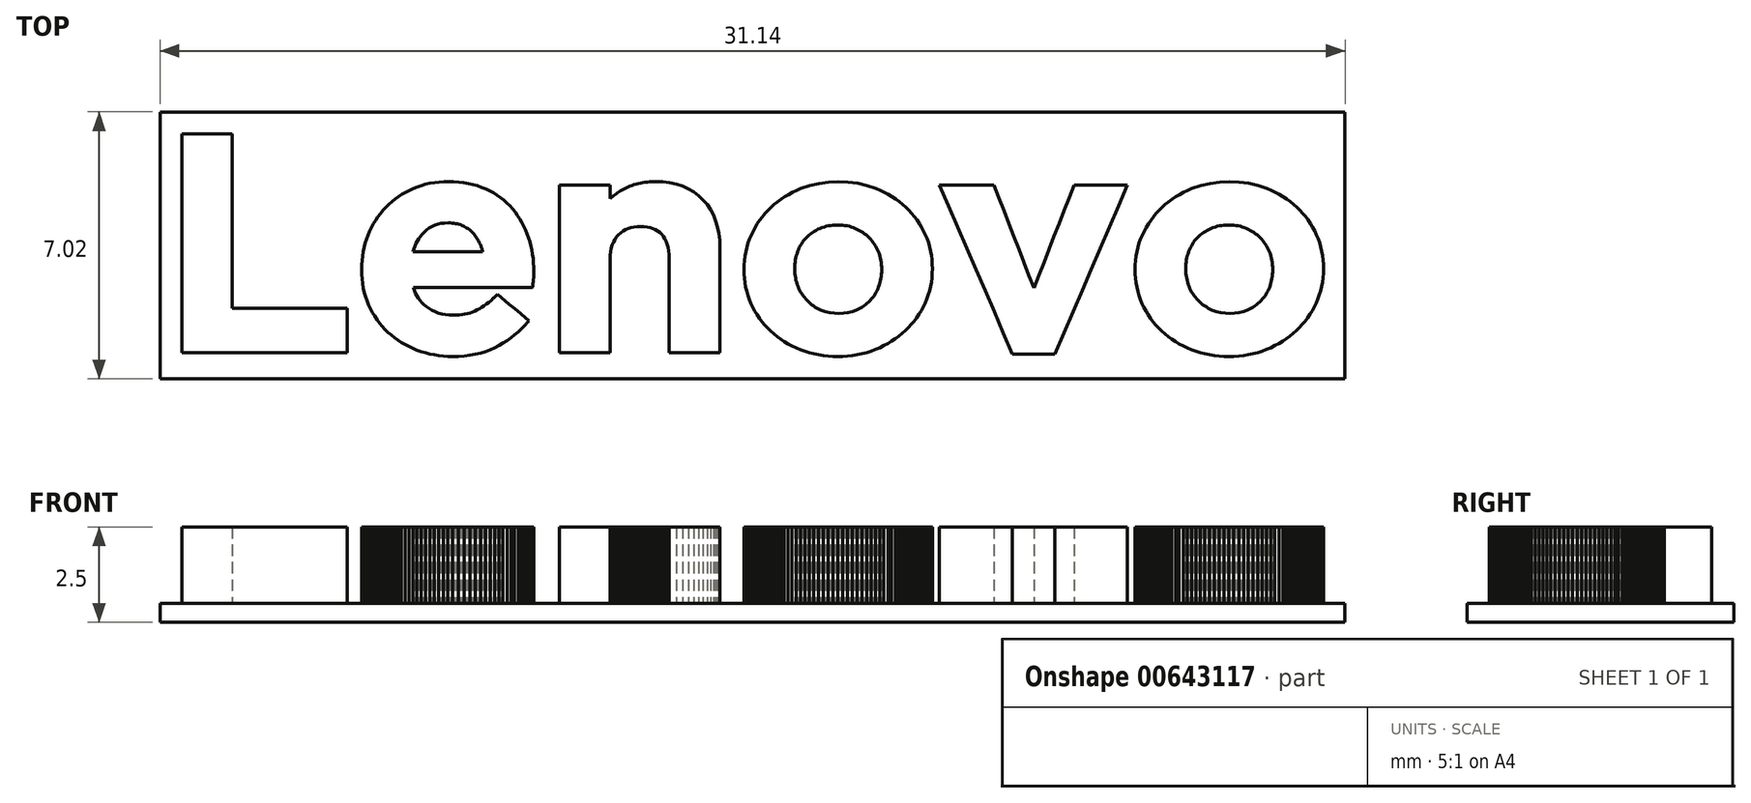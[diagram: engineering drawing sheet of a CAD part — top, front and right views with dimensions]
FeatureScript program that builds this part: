
annotation { "Feature Type Name" : "Feature", "Feature Type Description" : "" }
export const myFeature = defineFeature(function(context is Context, id is Id, definition is map)
    precondition{}
    {
        {
            var Q0;
            Q0=qCreatedBy(makeId("Top.planeOp"),FACE);
            var sketch = newSketch(context, id + "F0", { "sketchPlane" : qUnion([Q0])});
            skLineSegment(sketch, "E0", {"start": v(-13.67, -1.65) * mm, "end": v(-13.67, -1.08) * mm});
            skLineSegment(sketch, "E1", {"start": v(-13.67, -1.08) * mm, "end": v(-13.67, -0.5) * mm});
            skLineSegment(sketch, "E2", {"start": v(-13.67, -0.5) * mm, "end": v(-13.67, 0.06) * mm});
            skLineSegment(sketch, "E3", {"start": v(-13.67, 0.06) * mm, "end": v(-13.67, 0.64) * mm});
            skLineSegment(sketch, "E4", {"start": v(-13.67, 0.64) * mm, "end": v(-13.67, 1.2) * mm});
            skLineSegment(sketch, "E5", {"start": v(-13.67, 1.2) * mm, "end": v(-13.67, 1.78) * mm});
            skLineSegment(sketch, "E6", {"start": v(-13.67, 1.78) * mm, "end": v(-13.67, 2.35) * mm});
            skLineSegment(sketch, "E7", {"start": v(-13.67, 2.35) * mm, "end": v(-13.67, 2.92) * mm});
            skLineSegment(sketch, "E8", {"start": v(-13.67, 2.92) * mm, "end": v(-13.83, 2.92) * mm});
            skLineSegment(sketch, "E9", {"start": v(-13.83, 2.92) * mm, "end": v(-14, 2.92) * mm});
            skLineSegment(sketch, "E10", {"start": v(-14, 2.92) * mm, "end": v(-14.17, 2.92) * mm});
            skLineSegment(sketch, "E11", {"start": v(-14.17, 2.92) * mm, "end": v(-14.33, 2.92) * mm});
            skLineSegment(sketch, "E12", {"start": v(-14.33, 2.92) * mm, "end": v(-14.5, 2.92) * mm});
            skLineSegment(sketch, "E13", {"start": v(-14.5, 2.92) * mm, "end": v(-14.67, 2.92) * mm});
            skLineSegment(sketch, "E14", {"start": v(-14.67, 2.92) * mm, "end": v(-14.83, 2.92) * mm});
            skLineSegment(sketch, "E15", {"start": v(-14.83, 2.92) * mm, "end": v(-15, 2.92) * mm});
            skLineSegment(sketch, "E16", {"start": v(-15, 2.92) * mm, "end": v(-15, 2.2) * mm});
            skLineSegment(sketch, "E17", {"start": v(-15, 2.2) * mm, "end": v(-15, 1.49) * mm});
            skLineSegment(sketch, "E18", {"start": v(-15, 1.49) * mm, "end": v(-15, 0.77) * mm});
            skLineSegment(sketch, "E19", {"start": v(-15, 0.77) * mm, "end": v(-15, 0.05) * mm});
            skLineSegment(sketch, "E20", {"start": v(-15, 0.05) * mm, "end": v(-15, -0.67) * mm});
            skLineSegment(sketch, "E21", {"start": v(-15, -0.67) * mm, "end": v(-15, -1.4) * mm});
            skLineSegment(sketch, "E22", {"start": v(-15, -1.4) * mm, "end": v(-15, -2.11) * mm});
            skLineSegment(sketch, "E23", {"start": v(-15, -2.11) * mm, "end": v(-15, -2.83) * mm});
            skLineSegment(sketch, "E24", {"start": v(-15, -2.83) * mm, "end": v(-14.46, -2.83) * mm});
            skLineSegment(sketch, "E25", {"start": v(-14.46, -2.83) * mm, "end": v(-13.91, -2.83) * mm});
            skLineSegment(sketch, "E26", {"start": v(-13.91, -2.83) * mm, "end": v(-13.37, -2.83) * mm});
            skLineSegment(sketch, "E27", {"start": v(-13.37, -2.83) * mm, "end": v(-12.82, -2.83) * mm});
            skLineSegment(sketch, "E28", {"start": v(-12.82, -2.83) * mm, "end": v(-12.28, -2.83) * mm});
            skLineSegment(sketch, "E29", {"start": v(-12.28, -2.83) * mm, "end": v(-11.74, -2.83) * mm});
            skLineSegment(sketch, "E30", {"start": v(-11.74, -2.83) * mm, "end": v(-11.2, -2.83) * mm});
            skLineSegment(sketch, "E31", {"start": v(-11.2, -2.83) * mm, "end": v(-10.65, -2.83) * mm});
            skLineSegment(sketch, "E32", {"start": v(-10.65, -2.83) * mm, "end": v(-10.65, -2.68) * mm});
            skLineSegment(sketch, "E33", {"start": v(-10.65, -2.68) * mm, "end": v(-10.65, -2.54) * mm});
            skLineSegment(sketch, "E34", {"start": v(-10.65, -2.54) * mm, "end": v(-10.65, -2.39) * mm});
            skLineSegment(sketch, "E35", {"start": v(-10.65, -2.39) * mm, "end": v(-10.65, -2.24) * mm});
            skLineSegment(sketch, "E36", {"start": v(-10.65, -2.24) * mm, "end": v(-10.65, -2.1) * mm});
            skLineSegment(sketch, "E37", {"start": v(-10.65, -2.1) * mm, "end": v(-10.65, -1.95) * mm});
            skLineSegment(sketch, "E38", {"start": v(-10.65, -1.95) * mm, "end": v(-10.65, -1.8) * mm});
            skLineSegment(sketch, "E39", {"start": v(-10.65, -1.8) * mm, "end": v(-10.65, -1.65) * mm});
            skLineSegment(sketch, "E40", {"start": v(-10.65, -1.65) * mm, "end": v(-11.02, -1.65) * mm});
            skLineSegment(sketch, "E41", {"start": v(-11.02, -1.65) * mm, "end": v(-11.4, -1.65) * mm});
            skLineSegment(sketch, "E42", {"start": v(-11.4, -1.65) * mm, "end": v(-11.78, -1.65) * mm});
            skLineSegment(sketch, "E43", {"start": v(-11.78, -1.65) * mm, "end": v(-12.16, -1.65) * mm});
            skLineSegment(sketch, "E44", {"start": v(-12.16, -1.65) * mm, "end": v(-12.54, -1.65) * mm});
            skLineSegment(sketch, "E45", {"start": v(-12.54, -1.65) * mm, "end": v(-12.91, -1.65) * mm});
            skLineSegment(sketch, "E46", {"start": v(-12.91, -1.65) * mm, "end": v(-13.3, -1.65) * mm});
            skLineSegment(sketch, "E47", {"start": v(-13.3, -1.65) * mm, "end": v(-13.67, -1.65) * mm});
            skLineSegment(sketch, "E48", {"start": v(-7.1, -0.18) * mm, "end": v(-7.32, -0.18) * mm});
            skLineSegment(sketch, "E49", {"start": v(-7.32, -0.18) * mm, "end": v(-7.55, -0.18) * mm});
            skLineSegment(sketch, "E50", {"start": v(-7.55, -0.18) * mm, "end": v(-7.78, -0.18) * mm});
            skLineSegment(sketch, "E51", {"start": v(-7.78, -0.18) * mm, "end": v(-8, -0.18) * mm});
            skLineSegment(sketch, "E52", {"start": v(-8, -0.18) * mm, "end": v(-8.24, -0.18) * mm});
            skLineSegment(sketch, "E53", {"start": v(-8.24, -0.18) * mm, "end": v(-8.47, -0.18) * mm});
            skLineSegment(sketch, "E54", {"start": v(-8.47, -0.18) * mm, "end": v(-8.7, -0.18) * mm});
            skLineSegment(sketch, "E55", {"start": v(-8.7, -0.18) * mm, "end": v(-8.92, -0.18) * mm});
            skLineSegment(sketch, "E56", {"start": v(-8.92, -0.18) * mm, "end": v(-8.9, -0.1) * mm});
            skLineSegment(sketch, "E57", {"start": v(-8.9, -0.1) * mm, "end": v(-8.88, -0.03) * mm});
            skLineSegment(sketch, "E58", {"start": v(-8.88, -0.03) * mm, "end": v(-8.85, 0.04) * mm});
            skLineSegment(sketch, "E59", {"start": v(-8.85, 0.04) * mm, "end": v(-8.81, 0.1) * mm});
            skLineSegment(sketch, "E60", {"start": v(-8.81, 0.1) * mm, "end": v(-8.77, 0.17) * mm});
            skLineSegment(sketch, "E61", {"start": v(-8.77, 0.17) * mm, "end": v(-8.73, 0.23) * mm});
            skLineSegment(sketch, "E62", {"start": v(-8.73, 0.23) * mm, "end": v(-8.69, 0.29) * mm});
            skLineSegment(sketch, "E63", {"start": v(-8.69, 0.29) * mm, "end": v(-8.64, 0.34) * mm});
            skLineSegment(sketch, "E64", {"start": v(-8.64, 0.34) * mm, "end": v(-8.57, 0.4) * mm});
            skLineSegment(sketch, "E65", {"start": v(-8.57, 0.4) * mm, "end": v(-8.5, 0.45) * mm});
            skLineSegment(sketch, "E66", {"start": v(-8.5, 0.45) * mm, "end": v(-8.43, 0.5) * mm});
            skLineSegment(sketch, "E67", {"start": v(-8.43, 0.5) * mm, "end": v(-8.35, 0.53) * mm});
            skLineSegment(sketch, "E68", {"start": v(-8.35, 0.53) * mm, "end": v(-8.27, 0.55) * mm});
            skLineSegment(sketch, "E69", {"start": v(-8.27, 0.55) * mm, "end": v(-8.19, 0.57) * mm});
            skLineSegment(sketch, "E70", {"start": v(-8.19, 0.57) * mm, "end": v(-8.1, 0.58) * mm});
            skLineSegment(sketch, "E71", {"start": v(-8.1, 0.58) * mm, "end": v(-8, 0.59) * mm});
            skLineSegment(sketch, "E72", {"start": v(-8, 0.59) * mm, "end": v(-7.95, 0.59) * mm});
            skLineSegment(sketch, "E73", {"start": v(-7.95, 0.59) * mm, "end": v(-7.9, 0.58) * mm});
            skLineSegment(sketch, "E74", {"start": v(-7.9, 0.58) * mm, "end": v(-7.85, 0.58) * mm});
            skLineSegment(sketch, "E75", {"start": v(-7.85, 0.58) * mm, "end": v(-7.8, 0.57) * mm});
            skLineSegment(sketch, "E76", {"start": v(-7.8, 0.57) * mm, "end": v(-7.76, 0.56) * mm});
            skLineSegment(sketch, "E77", {"start": v(-7.76, 0.56) * mm, "end": v(-7.71, 0.55) * mm});
            skLineSegment(sketch, "E78", {"start": v(-7.71, 0.55) * mm, "end": v(-7.67, 0.53) * mm});
            skLineSegment(sketch, "E79", {"start": v(-7.67, 0.53) * mm, "end": v(-7.63, 0.52) * mm});
            skLineSegment(sketch, "E80", {"start": v(-7.63, 0.52) * mm, "end": v(-7.59, 0.5) * mm});
            skLineSegment(sketch, "E81", {"start": v(-7.59, 0.5) * mm, "end": v(-7.55, 0.48) * mm});
            skLineSegment(sketch, "E82", {"start": v(-7.55, 0.48) * mm, "end": v(-7.51, 0.46) * mm});
            skLineSegment(sketch, "E83", {"start": v(-7.51, 0.46) * mm, "end": v(-7.48, 0.43) * mm});
            skLineSegment(sketch, "E84", {"start": v(-7.48, 0.43) * mm, "end": v(-7.44, 0.4) * mm});
            skLineSegment(sketch, "E85", {"start": v(-7.44, 0.4) * mm, "end": v(-7.41, 0.38) * mm});
            skLineSegment(sketch, "E86", {"start": v(-7.41, 0.38) * mm, "end": v(-7.38, 0.35) * mm});
            skLineSegment(sketch, "E87", {"start": v(-7.38, 0.35) * mm, "end": v(-7.35, 0.32) * mm});
            skLineSegment(sketch, "E88", {"start": v(-7.35, 0.32) * mm, "end": v(-7.32, 0.3) * mm});
            skLineSegment(sketch, "E89", {"start": v(-7.32, 0.3) * mm, "end": v(-7.3, 0.26) * mm});
            skLineSegment(sketch, "E90", {"start": v(-7.3, 0.26) * mm, "end": v(-7.27, 0.23) * mm});
            skLineSegment(sketch, "E91", {"start": v(-7.27, 0.23) * mm, "end": v(-7.24, 0.2) * mm});
            skLineSegment(sketch, "E92", {"start": v(-7.24, 0.2) * mm, "end": v(-7.22, 0.15) * mm});
            skLineSegment(sketch, "E93", {"start": v(-7.22, 0.15) * mm, "end": v(-7.2, 0.11) * mm});
            skLineSegment(sketch, "E94", {"start": v(-7.2, 0.11) * mm, "end": v(-7.18, 0.07) * mm});
            skLineSegment(sketch, "E95", {"start": v(-7.18, 0.07) * mm, "end": v(-7.16, 0.03) * mm});
            skLineSegment(sketch, "E96", {"start": v(-7.16, 0.03) * mm, "end": v(-7.15, 0) * mm});
            skLineSegment(sketch, "E97", {"start": v(-7.15, 0) * mm, "end": v(-7.14, -0.02) * mm});
            skLineSegment(sketch, "E98", {"start": v(-7.14, -0.02) * mm, "end": v(-7.13, -0.04) * mm});
            skLineSegment(sketch, "E99", {"start": v(-7.13, -0.04) * mm, "end": v(-7.12, -0.07) * mm});
            skLineSegment(sketch, "E100", {"start": v(-7.12, -0.07) * mm, "end": v(-7.11, -0.1) * mm});
            skLineSegment(sketch, "E101", {"start": v(-7.11, -0.1) * mm, "end": v(-7.1, -0.12) * mm});
            skLineSegment(sketch, "E102", {"start": v(-7.1, -0.12) * mm, "end": v(-7.1, -0.15) * mm});
            skLineSegment(sketch, "E103", {"start": v(-7.1, -0.15) * mm, "end": v(-7.1, -0.18) * mm});
            skLineSegment(sketch, "E104", {"start": v(-5.89, 0.2) * mm, "end": v(-5.92, 0.3) * mm});
            skLineSegment(sketch, "E105", {"start": v(-5.92, 0.3) * mm, "end": v(-5.96, 0.4) * mm});
            skLineSegment(sketch, "E106", {"start": v(-5.96, 0.4) * mm, "end": v(-6.01, 0.5) * mm});
            skLineSegment(sketch, "E107", {"start": v(-6.01, 0.5) * mm, "end": v(-6.06, 0.6) * mm});
            skLineSegment(sketch, "E108", {"start": v(-6.06, 0.6) * mm, "end": v(-6.12, 0.7) * mm});
            skLineSegment(sketch, "E109", {"start": v(-6.12, 0.7) * mm, "end": v(-6.17, 0.78) * mm});
            skLineSegment(sketch, "E110", {"start": v(-6.17, 0.78) * mm, "end": v(-6.24, 0.87) * mm});
            skLineSegment(sketch, "E111", {"start": v(-6.24, 0.87) * mm, "end": v(-6.3, 0.95) * mm});
            skLineSegment(sketch, "E112", {"start": v(-6.3, 0.95) * mm, "end": v(-6.38, 1.03) * mm});
            skLineSegment(sketch, "E113", {"start": v(-6.38, 1.03) * mm, "end": v(-6.45, 1.11) * mm});
            skLineSegment(sketch, "E114", {"start": v(-6.45, 1.11) * mm, "end": v(-6.54, 1.18) * mm});
            skLineSegment(sketch, "E115", {"start": v(-6.54, 1.18) * mm, "end": v(-6.62, 1.25) * mm});
            skLineSegment(sketch, "E116", {"start": v(-6.62, 1.25) * mm, "end": v(-6.71, 1.31) * mm});
            skLineSegment(sketch, "E117", {"start": v(-6.71, 1.31) * mm, "end": v(-6.8, 1.37) * mm});
            skLineSegment(sketch, "E118", {"start": v(-6.8, 1.37) * mm, "end": v(-6.9, 1.43) * mm});
            skLineSegment(sketch, "E119", {"start": v(-6.9, 1.43) * mm, "end": v(-7.01, 1.48) * mm});
            skLineSegment(sketch, "E120", {"start": v(-7.01, 1.48) * mm, "end": v(-7.12, 1.52) * mm});
            skLineSegment(sketch, "E121", {"start": v(-7.12, 1.52) * mm, "end": v(-7.23, 1.56) * mm});
            skLineSegment(sketch, "E122", {"start": v(-7.23, 1.56) * mm, "end": v(-7.35, 1.6) * mm});
            skLineSegment(sketch, "E123", {"start": v(-7.35, 1.6) * mm, "end": v(-7.47, 1.62) * mm});
            skLineSegment(sketch, "E124", {"start": v(-7.47, 1.62) * mm, "end": v(-7.6, 1.65) * mm});
            skLineSegment(sketch, "E125", {"start": v(-7.6, 1.65) * mm, "end": v(-7.72, 1.66) * mm});
            skLineSegment(sketch, "E126", {"start": v(-7.72, 1.66) * mm, "end": v(-7.85, 1.67) * mm});
            skLineSegment(sketch, "E127", {"start": v(-7.85, 1.67) * mm, "end": v(-7.99, 1.67) * mm});
            skLineSegment(sketch, "E128", {"start": v(-7.99, 1.67) * mm, "end": v(-8.11, 1.67) * mm});
            skLineSegment(sketch, "E129", {"start": v(-8.11, 1.67) * mm, "end": v(-8.24, 1.66) * mm});
            skLineSegment(sketch, "E130", {"start": v(-8.24, 1.66) * mm, "end": v(-8.36, 1.65) * mm});
            skLineSegment(sketch, "E131", {"start": v(-8.36, 1.65) * mm, "end": v(-8.47, 1.63) * mm});
            skLineSegment(sketch, "E132", {"start": v(-8.47, 1.63) * mm, "end": v(-8.59, 1.6) * mm});
            skLineSegment(sketch, "E133", {"start": v(-8.59, 1.6) * mm, "end": v(-8.7, 1.57) * mm});
            skLineSegment(sketch, "E134", {"start": v(-8.7, 1.57) * mm, "end": v(-8.8, 1.53) * mm});
            skLineSegment(sketch, "E135", {"start": v(-8.8, 1.53) * mm, "end": v(-8.91, 1.5) * mm});
            skLineSegment(sketch, "E136", {"start": v(-8.91, 1.5) * mm, "end": v(-9.02, 1.44) * mm});
            skLineSegment(sketch, "E137", {"start": v(-9.02, 1.44) * mm, "end": v(-9.11, 1.4) * mm});
            skLineSegment(sketch, "E138", {"start": v(-9.11, 1.4) * mm, "end": v(-9.2, 1.34) * mm});
            skLineSegment(sketch, "E139", {"start": v(-9.2, 1.34) * mm, "end": v(-9.3, 1.28) * mm});
            skLineSegment(sketch, "E140", {"start": v(-9.3, 1.28) * mm, "end": v(-9.4, 1.21) * mm});
            skLineSegment(sketch, "E141", {"start": v(-9.4, 1.21) * mm, "end": v(-9.48, 1.14) * mm});
            skLineSegment(sketch, "E142", {"start": v(-9.48, 1.14) * mm, "end": v(-9.56, 1.07) * mm});
            skLineSegment(sketch, "E143", {"start": v(-9.56, 1.07) * mm, "end": v(-9.64, 1) * mm});
            skLineSegment(sketch, "E144", {"start": v(-9.64, 1) * mm, "end": v(-9.7, 0.92) * mm});
            skLineSegment(sketch, "E145", {"start": v(-9.7, 0.92) * mm, "end": v(-9.78, 0.83) * mm});
            skLineSegment(sketch, "E146", {"start": v(-9.78, 0.83) * mm, "end": v(-9.84, 0.75) * mm});
            skLineSegment(sketch, "E147", {"start": v(-9.84, 0.75) * mm, "end": v(-9.9, 0.66) * mm});
            skLineSegment(sketch, "E148", {"start": v(-9.9, 0.66) * mm, "end": v(-9.96, 0.56) * mm});
            skLineSegment(sketch, "E149", {"start": v(-9.96, 0.56) * mm, "end": v(-10.02, 0.47) * mm});
            skLineSegment(sketch, "E150", {"start": v(-10.02, 0.47) * mm, "end": v(-10.06, 0.37) * mm});
            skLineSegment(sketch, "E151", {"start": v(-10.06, 0.37) * mm, "end": v(-10.1, 0.27) * mm});
            skLineSegment(sketch, "E152", {"start": v(-10.1, 0.27) * mm, "end": v(-10.15, 0.16) * mm});
            skLineSegment(sketch, "E153", {"start": v(-10.15, 0.16) * mm, "end": v(-10.18, 0.05) * mm});
            skLineSegment(sketch, "E154", {"start": v(-10.18, 0.05) * mm, "end": v(-10.2, -0.05) * mm});
            skLineSegment(sketch, "E155", {"start": v(-10.2, -0.05) * mm, "end": v(-10.23, -0.17) * mm});
            skLineSegment(sketch, "E156", {"start": v(-10.23, -0.17) * mm, "end": v(-10.25, -0.28) * mm});
            skLineSegment(sketch, "E157", {"start": v(-10.25, -0.28) * mm, "end": v(-10.26, -0.4) * mm});
            skLineSegment(sketch, "E158", {"start": v(-10.26, -0.4) * mm, "end": v(-10.27, -0.52) * mm});
            skLineSegment(sketch, "E159", {"start": v(-10.27, -0.52) * mm, "end": v(-10.27, -0.64) * mm});
            skLineSegment(sketch, "E160", {"start": v(-10.27, -0.64) * mm, "end": v(-10.27, -0.76) * mm});
            skLineSegment(sketch, "E161", {"start": v(-10.27, -0.76) * mm, "end": v(-10.26, -0.88) * mm});
            skLineSegment(sketch, "E162", {"start": v(-10.26, -0.88) * mm, "end": v(-10.25, -1) * mm});
            skLineSegment(sketch, "E163", {"start": v(-10.25, -1) * mm, "end": v(-10.23, -1.12) * mm});
            skLineSegment(sketch, "E164", {"start": v(-10.23, -1.12) * mm, "end": v(-10.2, -1.24) * mm});
            skLineSegment(sketch, "E165", {"start": v(-10.2, -1.24) * mm, "end": v(-10.17, -1.35) * mm});
            skLineSegment(sketch, "E166", {"start": v(-10.17, -1.35) * mm, "end": v(-10.13, -1.46) * mm});
            skLineSegment(sketch, "E167", {"start": v(-10.13, -1.46) * mm, "end": v(-10.1, -1.56) * mm});
            skLineSegment(sketch, "E168", {"start": v(-10.1, -1.56) * mm, "end": v(-10.04, -1.67) * mm});
            skLineSegment(sketch, "E169", {"start": v(-10.04, -1.67) * mm, "end": v(-9.99, -1.77) * mm});
            skLineSegment(sketch, "E170", {"start": v(-9.99, -1.77) * mm, "end": v(-9.93, -1.86) * mm});
            skLineSegment(sketch, "E171", {"start": v(-9.93, -1.86) * mm, "end": v(-9.87, -1.96) * mm});
            skLineSegment(sketch, "E172", {"start": v(-9.87, -1.96) * mm, "end": v(-9.8, -2.04) * mm});
            skLineSegment(sketch, "E173", {"start": v(-9.8, -2.04) * mm, "end": v(-9.73, -2.13) * mm});
            skLineSegment(sketch, "E174", {"start": v(-9.73, -2.13) * mm, "end": v(-9.66, -2.21) * mm});
            skLineSegment(sketch, "E175", {"start": v(-9.66, -2.21) * mm, "end": v(-9.58, -2.29) * mm});
            skLineSegment(sketch, "E176", {"start": v(-9.58, -2.29) * mm, "end": v(-9.5, -2.36) * mm});
            skLineSegment(sketch, "E177", {"start": v(-9.5, -2.36) * mm, "end": v(-9.41, -2.43) * mm});
            skLineSegment(sketch, "E178", {"start": v(-9.41, -2.43) * mm, "end": v(-9.32, -2.5) * mm});
            skLineSegment(sketch, "E179", {"start": v(-9.32, -2.5) * mm, "end": v(-9.23, -2.56) * mm});
            skLineSegment(sketch, "E180", {"start": v(-9.23, -2.56) * mm, "end": v(-9.13, -2.61) * mm});
            skLineSegment(sketch, "E181", {"start": v(-9.13, -2.61) * mm, "end": v(-9.03, -2.66) * mm});
            skLineSegment(sketch, "E182", {"start": v(-9.03, -2.66) * mm, "end": v(-8.93, -2.71) * mm});
            skLineSegment(sketch, "E183", {"start": v(-8.93, -2.71) * mm, "end": v(-8.82, -2.76) * mm});
            skLineSegment(sketch, "E184", {"start": v(-8.82, -2.76) * mm, "end": v(-8.7, -2.8) * mm});
            skLineSegment(sketch, "E185", {"start": v(-8.7, -2.8) * mm, "end": v(-8.6, -2.83) * mm});
            skLineSegment(sketch, "E186", {"start": v(-8.6, -2.83) * mm, "end": v(-8.48, -2.86) * mm});
            skLineSegment(sketch, "E187", {"start": v(-8.48, -2.86) * mm, "end": v(-8.37, -2.88) * mm});
            skLineSegment(sketch, "E188", {"start": v(-8.37, -2.88) * mm, "end": v(-8.25, -2.9) * mm});
            skLineSegment(sketch, "E189", {"start": v(-8.25, -2.9) * mm, "end": v(-8.13, -2.91) * mm});
            skLineSegment(sketch, "E190", {"start": v(-8.13, -2.91) * mm, "end": v(-8, -2.92) * mm});
            skLineSegment(sketch, "E191", {"start": v(-8, -2.92) * mm, "end": v(-7.88, -2.92) * mm});
            skLineSegment(sketch, "E192", {"start": v(-7.88, -2.92) * mm, "end": v(-7.73, -2.92) * mm});
            skLineSegment(sketch, "E193", {"start": v(-7.73, -2.92) * mm, "end": v(-7.57, -2.9) * mm});
            skLineSegment(sketch, "E194", {"start": v(-7.57, -2.9) * mm, "end": v(-7.43, -2.9) * mm});
            skLineSegment(sketch, "E195", {"start": v(-7.43, -2.9) * mm, "end": v(-7.29, -2.87) * mm});
            skLineSegment(sketch, "E196", {"start": v(-7.29, -2.87) * mm, "end": v(-7.15, -2.83) * mm});
            skLineSegment(sketch, "E197", {"start": v(-7.15, -2.83) * mm, "end": v(-7.02, -2.8) * mm});
            skLineSegment(sketch, "E198", {"start": v(-7.02, -2.8) * mm, "end": v(-6.9, -2.75) * mm});
            skLineSegment(sketch, "E199", {"start": v(-6.9, -2.75) * mm, "end": v(-6.78, -2.7) * mm});
            skLineSegment(sketch, "E200", {"start": v(-6.78, -2.7) * mm, "end": v(-6.66, -2.64) * mm});
            skLineSegment(sketch, "E201", {"start": v(-6.66, -2.64) * mm, "end": v(-6.56, -2.57) * mm});
            skLineSegment(sketch, "E202", {"start": v(-6.56, -2.57) * mm, "end": v(-6.45, -2.5) * mm});
            skLineSegment(sketch, "E203", {"start": v(-6.45, -2.5) * mm, "end": v(-6.35, -2.43) * mm});
            skLineSegment(sketch, "E204", {"start": v(-6.35, -2.43) * mm, "end": v(-6.25, -2.36) * mm});
            skLineSegment(sketch, "E205", {"start": v(-6.25, -2.36) * mm, "end": v(-6.16, -2.28) * mm});
            skLineSegment(sketch, "E206", {"start": v(-6.16, -2.28) * mm, "end": v(-6.07, -2.19) * mm});
            skLineSegment(sketch, "E207", {"start": v(-6.07, -2.19) * mm, "end": v(-5.98, -2.1) * mm});
            skLineSegment(sketch, "E208", {"start": v(-5.98, -2.1) * mm, "end": v(-5.97, -2.08) * mm});
            skLineSegment(sketch, "E209", {"start": v(-5.97, -2.08) * mm, "end": v(-5.96, -2.07) * mm});
            skLineSegment(sketch, "E210", {"start": v(-5.96, -2.07) * mm, "end": v(-5.94, -2.06) * mm});
            skLineSegment(sketch, "E211", {"start": v(-5.94, -2.06) * mm, "end": v(-5.93, -2.04) * mm});
            skLineSegment(sketch, "E212", {"start": v(-5.93, -2.04) * mm, "end": v(-5.92, -2.03) * mm});
            skLineSegment(sketch, "E213", {"start": v(-5.92, -2.03) * mm, "end": v(-5.9, -2.01) * mm});
            skLineSegment(sketch, "E214", {"start": v(-5.9, -2.01) * mm, "end": v(-5.9, -2) * mm});
            skLineSegment(sketch, "E215", {"start": v(-5.9, -2) * mm, "end": v(-5.88, -1.98) * mm});
            skLineSegment(sketch, "E216", {"start": v(-5.88, -1.98) * mm, "end": v(-5.98, -1.9) * mm});
            skLineSegment(sketch, "E217", {"start": v(-5.98, -1.9) * mm, "end": v(-6.08, -1.8) * mm});
            skLineSegment(sketch, "E218", {"start": v(-6.08, -1.8) * mm, "end": v(-6.19, -1.72) * mm});
            skLineSegment(sketch, "E219", {"start": v(-6.19, -1.72) * mm, "end": v(-6.29, -1.64) * mm});
            skLineSegment(sketch, "E220", {"start": v(-6.29, -1.64) * mm, "end": v(-6.4, -1.55) * mm});
            skLineSegment(sketch, "E221", {"start": v(-6.4, -1.55) * mm, "end": v(-6.5, -1.46) * mm});
            skLineSegment(sketch, "E222", {"start": v(-6.5, -1.46) * mm, "end": v(-6.6, -1.38) * mm});
            skLineSegment(sketch, "E223", {"start": v(-6.6, -1.38) * mm, "end": v(-6.7, -1.3) * mm});
            skLineSegment(sketch, "E224", {"start": v(-6.7, -1.3) * mm, "end": v(-6.71, -1.3) * mm});
            skLineSegment(sketch, "E225", {"start": v(-6.71, -1.3) * mm, "end": v(-6.73, -1.32) * mm});
            skLineSegment(sketch, "E226", {"start": v(-6.73, -1.32) * mm, "end": v(-6.74, -1.33) * mm});
            skLineSegment(sketch, "E227", {"start": v(-6.74, -1.33) * mm, "end": v(-6.75, -1.34) * mm});
            skLineSegment(sketch, "E228", {"start": v(-6.75, -1.34) * mm, "end": v(-6.77, -1.36) * mm});
            skLineSegment(sketch, "E229", {"start": v(-6.77, -1.36) * mm, "end": v(-6.78, -1.37) * mm});
            skLineSegment(sketch, "E230", {"start": v(-6.78, -1.37) * mm, "end": v(-6.8, -1.38) * mm});
            skLineSegment(sketch, "E231", {"start": v(-6.8, -1.38) * mm, "end": v(-6.8, -1.4) * mm});
            skLineSegment(sketch, "E232", {"start": v(-6.8, -1.4) * mm, "end": v(-6.87, -1.45) * mm});
            skLineSegment(sketch, "E233", {"start": v(-6.87, -1.45) * mm, "end": v(-6.93, -1.5) * mm});
            skLineSegment(sketch, "E234", {"start": v(-6.93, -1.5) * mm, "end": v(-7, -1.55) * mm});
            skLineSegment(sketch, "E235", {"start": v(-7, -1.55) * mm, "end": v(-7.05, -1.6) * mm});
            skLineSegment(sketch, "E236", {"start": v(-7.05, -1.6) * mm, "end": v(-7.11, -1.63) * mm});
            skLineSegment(sketch, "E237", {"start": v(-7.11, -1.63) * mm, "end": v(-7.18, -1.67) * mm});
            skLineSegment(sketch, "E238", {"start": v(-7.18, -1.67) * mm, "end": v(-7.24, -1.7) * mm});
            skLineSegment(sketch, "E239", {"start": v(-7.24, -1.7) * mm, "end": v(-7.3, -1.73) * mm});
            skLineSegment(sketch, "E240", {"start": v(-7.3, -1.73) * mm, "end": v(-7.36, -1.76) * mm});
            skLineSegment(sketch, "E241", {"start": v(-7.36, -1.76) * mm, "end": v(-7.42, -1.78) * mm});
            skLineSegment(sketch, "E242", {"start": v(-7.42, -1.78) * mm, "end": v(-7.49, -1.8) * mm});
            skLineSegment(sketch, "E243", {"start": v(-7.49, -1.8) * mm, "end": v(-7.56, -1.81) * mm});
            skLineSegment(sketch, "E244", {"start": v(-7.56, -1.81) * mm, "end": v(-7.63, -1.82) * mm});
            skLineSegment(sketch, "E245", {"start": v(-7.63, -1.82) * mm, "end": v(-7.7, -1.83) * mm});
            skLineSegment(sketch, "E246", {"start": v(-7.7, -1.83) * mm, "end": v(-7.79, -1.84) * mm});
            skLineSegment(sketch, "E247", {"start": v(-7.79, -1.84) * mm, "end": v(-7.87, -1.84) * mm});
            skLineSegment(sketch, "E248", {"start": v(-7.87, -1.84) * mm, "end": v(-7.97, -1.84) * mm});
            skLineSegment(sketch, "E249", {"start": v(-7.97, -1.84) * mm, "end": v(-8.07, -1.82) * mm});
            skLineSegment(sketch, "E250", {"start": v(-8.07, -1.82) * mm, "end": v(-8.17, -1.8) * mm});
            skLineSegment(sketch, "E251", {"start": v(-8.17, -1.8) * mm, "end": v(-8.26, -1.78) * mm});
            skLineSegment(sketch, "E252", {"start": v(-8.26, -1.78) * mm, "end": v(-8.35, -1.75) * mm});
            skLineSegment(sketch, "E253", {"start": v(-8.35, -1.75) * mm, "end": v(-8.43, -1.7) * mm});
            skLineSegment(sketch, "E254", {"start": v(-8.43, -1.7) * mm, "end": v(-8.5, -1.66) * mm});
            skLineSegment(sketch, "E255", {"start": v(-8.5, -1.66) * mm, "end": v(-8.58, -1.6) * mm});
            skLineSegment(sketch, "E256", {"start": v(-8.58, -1.6) * mm, "end": v(-8.64, -1.56) * mm});
            skLineSegment(sketch, "E257", {"start": v(-8.64, -1.56) * mm, "end": v(-8.7, -1.5) * mm});
            skLineSegment(sketch, "E258", {"start": v(-8.7, -1.5) * mm, "end": v(-8.74, -1.45) * mm});
            skLineSegment(sketch, "E259", {"start": v(-8.74, -1.45) * mm, "end": v(-8.78, -1.4) * mm});
            skLineSegment(sketch, "E260", {"start": v(-8.78, -1.4) * mm, "end": v(-8.82, -1.33) * mm});
            skLineSegment(sketch, "E261", {"start": v(-8.82, -1.33) * mm, "end": v(-8.85, -1.26) * mm});
            skLineSegment(sketch, "E262", {"start": v(-8.85, -1.26) * mm, "end": v(-8.88, -1.19) * mm});
            skLineSegment(sketch, "E263", {"start": v(-8.88, -1.19) * mm, "end": v(-8.91, -1.11) * mm});
            skLineSegment(sketch, "E264", {"start": v(-8.91, -1.11) * mm, "end": v(-8.52, -1.11) * mm});
            skLineSegment(sketch, "E265", {"start": v(-8.52, -1.11) * mm, "end": v(-8.13, -1.11) * mm});
            skLineSegment(sketch, "E266", {"start": v(-8.13, -1.11) * mm, "end": v(-7.74, -1.11) * mm});
            skLineSegment(sketch, "E267", {"start": v(-7.74, -1.11) * mm, "end": v(-7.35, -1.11) * mm});
            skLineSegment(sketch, "E268", {"start": v(-7.35, -1.11) * mm, "end": v(-6.96, -1.11) * mm});
            skLineSegment(sketch, "E269", {"start": v(-6.96, -1.11) * mm, "end": v(-6.56, -1.11) * mm});
            skLineSegment(sketch, "E270", {"start": v(-6.56, -1.11) * mm, "end": v(-6.17, -1.11) * mm});
            skLineSegment(sketch, "E271", {"start": v(-6.17, -1.11) * mm, "end": v(-5.78, -1.11) * mm});
            skLineSegment(sketch, "E272", {"start": v(-5.78, -1.11) * mm, "end": v(-5.78, -1.1) * mm});
            skLineSegment(sketch, "E273", {"start": v(-5.78, -1.1) * mm, "end": v(-5.78, -1.08) * mm});
            skLineSegment(sketch, "E274", {"start": v(-5.78, -1.08) * mm, "end": v(-5.78, -1.06) * mm});
            skLineSegment(sketch, "E275", {"start": v(-5.78, -1.06) * mm, "end": v(-5.77, -1.04) * mm});
            skLineSegment(sketch, "E276", {"start": v(-5.77, -1.04) * mm, "end": v(-5.77, -1.03) * mm});
            skLineSegment(sketch, "E277", {"start": v(-5.77, -1.03) * mm, "end": v(-5.77, -1) * mm});
            skLineSegment(sketch, "E278", {"start": v(-5.77, -1) * mm, "end": v(-5.77, -1) * mm});
            skLineSegment(sketch, "E279", {"start": v(-5.77, -1) * mm, "end": v(-5.76, -0.97) * mm});
            skLineSegment(sketch, "E280", {"start": v(-5.76, -0.97) * mm, "end": v(-5.76, -0.95) * mm});
            skLineSegment(sketch, "E281", {"start": v(-5.76, -0.95) * mm, "end": v(-5.76, -0.94) * mm});
            skLineSegment(sketch, "E282", {"start": v(-5.76, -0.94) * mm, "end": v(-5.76, -0.92) * mm});
            skLineSegment(sketch, "E283", {"start": v(-5.76, -0.92) * mm, "end": v(-5.76, -0.9) * mm});
            skLineSegment(sketch, "E284", {"start": v(-5.76, -0.9) * mm, "end": v(-5.76, -0.88) * mm});
            skLineSegment(sketch, "E285", {"start": v(-5.76, -0.88) * mm, "end": v(-5.75, -0.86) * mm});
            skLineSegment(sketch, "E286", {"start": v(-5.75, -0.86) * mm, "end": v(-5.75, -0.85) * mm});
            skLineSegment(sketch, "E287", {"start": v(-5.75, -0.85) * mm, "end": v(-5.75, -0.83) * mm});
            skLineSegment(sketch, "E288", {"start": v(-5.75, -0.83) * mm, "end": v(-5.75, -0.81) * mm});
            skLineSegment(sketch, "E289", {"start": v(-5.75, -0.81) * mm, "end": v(-5.75, -0.8) * mm});
            skLineSegment(sketch, "E290", {"start": v(-5.75, -0.8) * mm, "end": v(-5.75, -0.78) * mm});
            skLineSegment(sketch, "E291", {"start": v(-5.75, -0.78) * mm, "end": v(-5.75, -0.76) * mm});
            skLineSegment(sketch, "E292", {"start": v(-5.75, -0.76) * mm, "end": v(-5.75, -0.74) * mm});
            skLineSegment(sketch, "E293", {"start": v(-5.75, -0.74) * mm, "end": v(-5.75, -0.73) * mm});
            skLineSegment(sketch, "E294", {"start": v(-5.75, -0.73) * mm, "end": v(-5.75, -0.7) * mm});
            skLineSegment(sketch, "E295", {"start": v(-5.75, -0.7) * mm, "end": v(-5.75, -0.7) * mm});
            skLineSegment(sketch, "E296", {"start": v(-5.75, -0.7) * mm, "end": v(-5.75, -0.58) * mm});
            skLineSegment(sketch, "E297", {"start": v(-5.75, -0.58) * mm, "end": v(-5.76, -0.46) * mm});
            skLineSegment(sketch, "E298", {"start": v(-5.76, -0.46) * mm, "end": v(-5.77, -0.35) * mm});
            skLineSegment(sketch, "E299", {"start": v(-5.77, -0.35) * mm, "end": v(-5.78, -0.24) * mm});
            skLineSegment(sketch, "E300", {"start": v(-5.78, -0.24) * mm, "end": v(-5.8, -0.13) * mm});
            skLineSegment(sketch, "E301", {"start": v(-5.8, -0.13) * mm, "end": v(-5.83, -0.02) * mm});
            skLineSegment(sketch, "E302", {"start": v(-5.83, -0.02) * mm, "end": v(-5.85, 0.1) * mm});
            skLineSegment(sketch, "E303", {"start": v(-5.85, 0.1) * mm, "end": v(-5.89, 0.2) * mm});
            skLineSegment(sketch, "E304", {"start": v(-1.3, 1.2) * mm, "end": v(-1.42, 1.3) * mm});
            skLineSegment(sketch, "E305", {"start": v(-1.42, 1.3) * mm, "end": v(-1.55, 1.4) * mm});
            skLineSegment(sketch, "E306", {"start": v(-1.55, 1.4) * mm, "end": v(-1.69, 1.48) * mm});
            skLineSegment(sketch, "E307", {"start": v(-1.69, 1.48) * mm, "end": v(-1.84, 1.55) * mm});
            skLineSegment(sketch, "E308", {"start": v(-1.84, 1.55) * mm, "end": v(-2, 1.6) * mm});
            skLineSegment(sketch, "E309", {"start": v(-2, 1.6) * mm, "end": v(-2.18, 1.64) * mm});
            skLineSegment(sketch, "E310", {"start": v(-2.18, 1.64) * mm, "end": v(-2.36, 1.67) * mm});
            skLineSegment(sketch, "E311", {"start": v(-2.36, 1.67) * mm, "end": v(-2.56, 1.67) * mm});
            skLineSegment(sketch, "E312", {"start": v(-2.56, 1.67) * mm, "end": v(-2.63, 1.67) * mm});
            skLineSegment(sketch, "E313", {"start": v(-2.63, 1.67) * mm, "end": v(-2.7, 1.67) * mm});
            skLineSegment(sketch, "E314", {"start": v(-2.7, 1.67) * mm, "end": v(-2.76, 1.66) * mm});
            skLineSegment(sketch, "E315", {"start": v(-2.76, 1.66) * mm, "end": v(-2.83, 1.66) * mm});
            skLineSegment(sketch, "E316", {"start": v(-2.83, 1.66) * mm, "end": v(-2.89, 1.65) * mm});
            skLineSegment(sketch, "E317", {"start": v(-2.89, 1.65) * mm, "end": v(-2.95, 1.64) * mm});
            skLineSegment(sketch, "E318", {"start": v(-2.95, 1.64) * mm, "end": v(-3, 1.62) * mm});
            skLineSegment(sketch, "E319", {"start": v(-3, 1.62) * mm, "end": v(-3.06, 1.6) * mm});
            skLineSegment(sketch, "E320", {"start": v(-3.06, 1.6) * mm, "end": v(-3.12, 1.59) * mm});
            skLineSegment(sketch, "E321", {"start": v(-3.12, 1.59) * mm, "end": v(-3.17, 1.57) * mm});
            skLineSegment(sketch, "E322", {"start": v(-3.17, 1.57) * mm, "end": v(-3.22, 1.55) * mm});
            skLineSegment(sketch, "E323", {"start": v(-3.22, 1.55) * mm, "end": v(-3.28, 1.53) * mm});
            skLineSegment(sketch, "E324", {"start": v(-3.28, 1.53) * mm, "end": v(-3.33, 1.5) * mm});
            skLineSegment(sketch, "E325", {"start": v(-3.33, 1.5) * mm, "end": v(-3.38, 1.48) * mm});
            skLineSegment(sketch, "E326", {"start": v(-3.38, 1.48) * mm, "end": v(-3.43, 1.46) * mm});
            skLineSegment(sketch, "E327", {"start": v(-3.43, 1.46) * mm, "end": v(-3.47, 1.43) * mm});
            skLineSegment(sketch, "E328", {"start": v(-3.47, 1.43) * mm, "end": v(-3.51, 1.4) * mm});
            skLineSegment(sketch, "E329", {"start": v(-3.51, 1.4) * mm, "end": v(-3.55, 1.38) * mm});
            skLineSegment(sketch, "E330", {"start": v(-3.55, 1.38) * mm, "end": v(-3.58, 1.36) * mm});
            skLineSegment(sketch, "E331", {"start": v(-3.58, 1.36) * mm, "end": v(-3.62, 1.33) * mm});
            skLineSegment(sketch, "E332", {"start": v(-3.62, 1.33) * mm, "end": v(-3.65, 1.3) * mm});
            skLineSegment(sketch, "E333", {"start": v(-3.65, 1.3) * mm, "end": v(-3.68, 1.28) * mm});
            skLineSegment(sketch, "E334", {"start": v(-3.68, 1.28) * mm, "end": v(-3.71, 1.25) * mm});
            skLineSegment(sketch, "E335", {"start": v(-3.71, 1.25) * mm, "end": v(-3.74, 1.22) * mm});
            skLineSegment(sketch, "E336", {"start": v(-3.74, 1.22) * mm, "end": v(-3.74, 1.27) * mm});
            skLineSegment(sketch, "E337", {"start": v(-3.74, 1.27) * mm, "end": v(-3.74, 1.32) * mm});
            skLineSegment(sketch, "E338", {"start": v(-3.74, 1.32) * mm, "end": v(-3.74, 1.36) * mm});
            skLineSegment(sketch, "E339", {"start": v(-3.74, 1.36) * mm, "end": v(-3.74, 1.4) * mm});
            skLineSegment(sketch, "E340", {"start": v(-3.74, 1.4) * mm, "end": v(-3.74, 1.45) * mm});
            skLineSegment(sketch, "E341", {"start": v(-3.74, 1.45) * mm, "end": v(-3.74, 1.5) * mm});
            skLineSegment(sketch, "E342", {"start": v(-3.74, 1.5) * mm, "end": v(-3.74, 1.54) * mm});
            skLineSegment(sketch, "E343", {"start": v(-3.74, 1.54) * mm, "end": v(-3.74, 1.59) * mm});
            skLineSegment(sketch, "E344", {"start": v(-3.74, 1.59) * mm, "end": v(-3.91, 1.59) * mm});
            skLineSegment(sketch, "E345", {"start": v(-3.91, 1.59) * mm, "end": v(-4.08, 1.59) * mm});
            skLineSegment(sketch, "E346", {"start": v(-4.08, 1.59) * mm, "end": v(-4.24, 1.59) * mm});
            skLineSegment(sketch, "E347", {"start": v(-4.24, 1.59) * mm, "end": v(-4.41, 1.59) * mm});
            skLineSegment(sketch, "E348", {"start": v(-4.41, 1.59) * mm, "end": v(-4.58, 1.59) * mm});
            skLineSegment(sketch, "E349", {"start": v(-4.58, 1.59) * mm, "end": v(-4.74, 1.59) * mm});
            skLineSegment(sketch, "E350", {"start": v(-4.74, 1.59) * mm, "end": v(-4.91, 1.59) * mm});
            skLineSegment(sketch, "E351", {"start": v(-4.91, 1.59) * mm, "end": v(-5.08, 1.59) * mm});
            skLineSegment(sketch, "E352", {"start": v(-5.08, 1.59) * mm, "end": v(-5.08, 1.04) * mm});
            skLineSegment(sketch, "E353", {"start": v(-5.08, 1.04) * mm, "end": v(-5.08, 0.48) * mm});
            skLineSegment(sketch, "E354", {"start": v(-5.08, 0.48) * mm, "end": v(-5.08, -0.07) * mm});
            skLineSegment(sketch, "E355", {"start": v(-5.08, -0.07) * mm, "end": v(-5.08, -0.62) * mm});
            skLineSegment(sketch, "E356", {"start": v(-5.08, -0.62) * mm, "end": v(-5.08, -1.17) * mm});
            skLineSegment(sketch, "E357", {"start": v(-5.08, -1.17) * mm, "end": v(-5.08, -1.73) * mm});
            skLineSegment(sketch, "E358", {"start": v(-5.08, -1.73) * mm, "end": v(-5.08, -2.28) * mm});
            skLineSegment(sketch, "E359", {"start": v(-5.08, -2.28) * mm, "end": v(-5.08, -2.83) * mm});
            skLineSegment(sketch, "E360", {"start": v(-5.08, -2.83) * mm, "end": v(-4.91, -2.83) * mm});
            skLineSegment(sketch, "E361", {"start": v(-4.91, -2.83) * mm, "end": v(-4.74, -2.83) * mm});
            skLineSegment(sketch, "E362", {"start": v(-4.74, -2.83) * mm, "end": v(-4.58, -2.83) * mm});
            skLineSegment(sketch, "E363", {"start": v(-4.58, -2.83) * mm, "end": v(-4.41, -2.83) * mm});
            skLineSegment(sketch, "E364", {"start": v(-4.41, -2.83) * mm, "end": v(-4.24, -2.83) * mm});
            skLineSegment(sketch, "E365", {"start": v(-4.24, -2.83) * mm, "end": v(-4.08, -2.83) * mm});
            skLineSegment(sketch, "E366", {"start": v(-4.08, -2.83) * mm, "end": v(-3.91, -2.83) * mm});
            skLineSegment(sketch, "E367", {"start": v(-3.91, -2.83) * mm, "end": v(-3.74, -2.83) * mm});
            skLineSegment(sketch, "E368", {"start": v(-3.74, -2.83) * mm, "end": v(-3.74, -2.52) * mm});
            skLineSegment(sketch, "E369", {"start": v(-3.74, -2.52) * mm, "end": v(-3.74, -2.21) * mm});
            skLineSegment(sketch, "E370", {"start": v(-3.74, -2.21) * mm, "end": v(-3.74, -1.9) * mm});
            skLineSegment(sketch, "E371", {"start": v(-3.74, -1.9) * mm, "end": v(-3.74, -1.6) * mm});
            skLineSegment(sketch, "E372", {"start": v(-3.74, -1.6) * mm, "end": v(-3.74, -1.29) * mm});
            skLineSegment(sketch, "E373", {"start": v(-3.74, -1.29) * mm, "end": v(-3.74, -0.98) * mm});
            skLineSegment(sketch, "E374", {"start": v(-3.74, -0.98) * mm, "end": v(-3.74, -0.67) * mm});
            skLineSegment(sketch, "E375", {"start": v(-3.74, -0.67) * mm, "end": v(-3.74, -0.36) * mm});
            skLineSegment(sketch, "E376", {"start": v(-3.74, -0.36) * mm, "end": v(-3.74, -0.26) * mm});
            skLineSegment(sketch, "E377", {"start": v(-3.74, -0.26) * mm, "end": v(-3.73, -0.17) * mm});
            skLineSegment(sketch, "E378", {"start": v(-3.73, -0.17) * mm, "end": v(-3.71, -0.08) * mm});
            skLineSegment(sketch, "E379", {"start": v(-3.71, -0.08) * mm, "end": v(-3.69, 0) * mm});
            skLineSegment(sketch, "E380", {"start": v(-3.69, 0) * mm, "end": v(-3.66, 0.08) * mm});
            skLineSegment(sketch, "E381", {"start": v(-3.66, 0.08) * mm, "end": v(-3.62, 0.15) * mm});
            skLineSegment(sketch, "E382", {"start": v(-3.62, 0.15) * mm, "end": v(-3.58, 0.22) * mm});
            skLineSegment(sketch, "E383", {"start": v(-3.58, 0.22) * mm, "end": v(-3.52, 0.28) * mm});
            skLineSegment(sketch, "E384", {"start": v(-3.52, 0.28) * mm, "end": v(-3.47, 0.33) * mm});
            skLineSegment(sketch, "E385", {"start": v(-3.47, 0.33) * mm, "end": v(-3.4, 0.37) * mm});
            skLineSegment(sketch, "E386", {"start": v(-3.4, 0.37) * mm, "end": v(-3.34, 0.41) * mm});
            skLineSegment(sketch, "E387", {"start": v(-3.34, 0.41) * mm, "end": v(-3.27, 0.44) * mm});
            skLineSegment(sketch, "E388", {"start": v(-3.27, 0.44) * mm, "end": v(-3.2, 0.46) * mm});
            skLineSegment(sketch, "E389", {"start": v(-3.2, 0.46) * mm, "end": v(-3.11, 0.48) * mm});
            skLineSegment(sketch, "E390", {"start": v(-3.11, 0.48) * mm, "end": v(-3.03, 0.5) * mm});
            skLineSegment(sketch, "E391", {"start": v(-3.03, 0.5) * mm, "end": v(-2.94, 0.5) * mm});
            skLineSegment(sketch, "E392", {"start": v(-2.94, 0.5) * mm, "end": v(-2.85, 0.5) * mm});
            skLineSegment(sketch, "E393", {"start": v(-2.85, 0.5) * mm, "end": v(-2.77, 0.48) * mm});
            skLineSegment(sketch, "E394", {"start": v(-2.77, 0.48) * mm, "end": v(-2.7, 0.47) * mm});
            skLineSegment(sketch, "E395", {"start": v(-2.7, 0.47) * mm, "end": v(-2.62, 0.44) * mm});
            skLineSegment(sketch, "E396", {"start": v(-2.62, 0.44) * mm, "end": v(-2.56, 0.42) * mm});
            skLineSegment(sketch, "E397", {"start": v(-2.56, 0.42) * mm, "end": v(-2.5, 0.38) * mm});
            skLineSegment(sketch, "E398", {"start": v(-2.5, 0.38) * mm, "end": v(-2.44, 0.34) * mm});
            skLineSegment(sketch, "E399", {"start": v(-2.44, 0.34) * mm, "end": v(-2.39, 0.3) * mm});
            skLineSegment(sketch, "E400", {"start": v(-2.39, 0.3) * mm, "end": v(-2.34, 0.23) * mm});
            skLineSegment(sketch, "E401", {"start": v(-2.34, 0.23) * mm, "end": v(-2.3, 0.17) * mm});
            skLineSegment(sketch, "E402", {"start": v(-2.3, 0.17) * mm, "end": v(-2.27, 0.1) * mm});
            skLineSegment(sketch, "E403", {"start": v(-2.27, 0.1) * mm, "end": v(-2.24, 0.02) * mm});
            skLineSegment(sketch, "E404", {"start": v(-2.24, 0.02) * mm, "end": v(-2.22, -0.06) * mm});
            skLineSegment(sketch, "E405", {"start": v(-2.22, -0.06) * mm, "end": v(-2.2, -0.15) * mm});
            skLineSegment(sketch, "E406", {"start": v(-2.2, -0.15) * mm, "end": v(-2.2, -0.25) * mm});
            skLineSegment(sketch, "E407", {"start": v(-2.2, -0.25) * mm, "end": v(-2.19, -0.35) * mm});
            skLineSegment(sketch, "E408", {"start": v(-2.19, -0.35) * mm, "end": v(-2.19, -0.66) * mm});
            skLineSegment(sketch, "E409", {"start": v(-2.19, -0.66) * mm, "end": v(-2.19, -0.97) * mm});
            skLineSegment(sketch, "E410", {"start": v(-2.19, -0.97) * mm, "end": v(-2.19, -1.28) * mm});
            skLineSegment(sketch, "E411", {"start": v(-2.19, -1.28) * mm, "end": v(-2.19, -1.59) * mm});
            skLineSegment(sketch, "E412", {"start": v(-2.19, -1.59) * mm, "end": v(-2.19, -1.9) * mm});
            skLineSegment(sketch, "E413", {"start": v(-2.19, -1.9) * mm, "end": v(-2.19, -2.2) * mm});
            skLineSegment(sketch, "E414", {"start": v(-2.19, -2.2) * mm, "end": v(-2.19, -2.52) * mm});
            skLineSegment(sketch, "E415", {"start": v(-2.19, -2.52) * mm, "end": v(-2.19, -2.83) * mm});
            skLineSegment(sketch, "E416", {"start": v(-2.19, -2.83) * mm, "end": v(-2.02, -2.83) * mm});
            skLineSegment(sketch, "E417", {"start": v(-2.02, -2.83) * mm, "end": v(-1.86, -2.83) * mm});
            skLineSegment(sketch, "E418", {"start": v(-1.86, -2.83) * mm, "end": v(-1.69, -2.83) * mm});
            skLineSegment(sketch, "E419", {"start": v(-1.69, -2.83) * mm, "end": v(-1.52, -2.83) * mm});
            skLineSegment(sketch, "E420", {"start": v(-1.52, -2.83) * mm, "end": v(-1.36, -2.83) * mm});
            skLineSegment(sketch, "E421", {"start": v(-1.36, -2.83) * mm, "end": v(-1.19, -2.83) * mm});
            skLineSegment(sketch, "E422", {"start": v(-1.19, -2.83) * mm, "end": v(-1.02, -2.83) * mm});
            skLineSegment(sketch, "E423", {"start": v(-1.02, -2.83) * mm, "end": v(-0.86, -2.83) * mm});
            skLineSegment(sketch, "E424", {"start": v(-0.86, -2.83) * mm, "end": v(-0.86, -2.48) * mm});
            skLineSegment(sketch, "E425", {"start": v(-0.86, -2.48) * mm, "end": v(-0.86, -2.14) * mm});
            skLineSegment(sketch, "E426", {"start": v(-0.86, -2.14) * mm, "end": v(-0.86, -1.8) * mm});
            skLineSegment(sketch, "E427", {"start": v(-0.86, -1.8) * mm, "end": v(-0.86, -1.45) * mm});
            skLineSegment(sketch, "E428", {"start": v(-0.86, -1.45) * mm, "end": v(-0.86, -1.1) * mm});
            skLineSegment(sketch, "E429", {"start": v(-0.86, -1.1) * mm, "end": v(-0.86, -0.75) * mm});
            skLineSegment(sketch, "E430", {"start": v(-0.86, -0.75) * mm, "end": v(-0.86, -0.4) * mm});
            skLineSegment(sketch, "E431", {"start": v(-0.86, -0.4) * mm, "end": v(-0.86, -0.06) * mm});
            skLineSegment(sketch, "E432", {"start": v(-0.86, -0.06) * mm, "end": v(-0.86, 0.13) * mm});
            skLineSegment(sketch, "E433", {"start": v(-0.86, 0.13) * mm, "end": v(-0.88, 0.3) * mm});
            skLineSegment(sketch, "E434", {"start": v(-0.88, 0.3) * mm, "end": v(-0.92, 0.48) * mm});
            skLineSegment(sketch, "E435", {"start": v(-0.92, 0.48) * mm, "end": v(-0.97, 0.64) * mm});
            skLineSegment(sketch, "E436", {"start": v(-0.97, 0.64) * mm, "end": v(-1.03, 0.8) * mm});
            skLineSegment(sketch, "E437", {"start": v(-1.03, 0.8) * mm, "end": v(-1.1, 0.94) * mm});
            skLineSegment(sketch, "E438", {"start": v(-1.1, 0.94) * mm, "end": v(-1.2, 1.07) * mm});
            skLineSegment(sketch, "E439", {"start": v(-1.2, 1.07) * mm, "end": v(-1.3, 1.2) * mm});
            skLineSegment(sketch, "E440", {"start": v(1.8, -1.7) * mm, "end": v(1.75, -1.68) * mm});
            skLineSegment(sketch, "E441", {"start": v(1.75, -1.68) * mm, "end": v(1.7, -1.65) * mm});
            skLineSegment(sketch, "E442", {"start": v(1.7, -1.65) * mm, "end": v(1.65, -1.62) * mm});
            skLineSegment(sketch, "E443", {"start": v(1.65, -1.62) * mm, "end": v(1.6, -1.6) * mm});
            skLineSegment(sketch, "E444", {"start": v(1.6, -1.6) * mm, "end": v(1.56, -1.56) * mm});
            skLineSegment(sketch, "E445", {"start": v(1.56, -1.56) * mm, "end": v(1.51, -1.53) * mm});
            skLineSegment(sketch, "E446", {"start": v(1.51, -1.53) * mm, "end": v(1.47, -1.5) * mm});
            skLineSegment(sketch, "E447", {"start": v(1.47, -1.5) * mm, "end": v(1.43, -1.45) * mm});
            skLineSegment(sketch, "E448", {"start": v(1.43, -1.45) * mm, "end": v(1.4, -1.41) * mm});
            skLineSegment(sketch, "E449", {"start": v(1.4, -1.41) * mm, "end": v(1.36, -1.37) * mm});
            skLineSegment(sketch, "E450", {"start": v(1.36, -1.37) * mm, "end": v(1.33, -1.32) * mm});
            skLineSegment(sketch, "E451", {"start": v(1.33, -1.32) * mm, "end": v(1.3, -1.28) * mm});
            skLineSegment(sketch, "E452", {"start": v(1.3, -1.28) * mm, "end": v(1.27, -1.23) * mm});
            skLineSegment(sketch, "E453", {"start": v(1.27, -1.23) * mm, "end": v(1.24, -1.18) * mm});
            skLineSegment(sketch, "E454", {"start": v(1.24, -1.18) * mm, "end": v(1.22, -1.13) * mm});
            skLineSegment(sketch, "E455", {"start": v(1.22, -1.13) * mm, "end": v(1.2, -1.08) * mm});
            skLineSegment(sketch, "E456", {"start": v(1.2, -1.08) * mm, "end": v(1.17, -1.03) * mm});
            skLineSegment(sketch, "E457", {"start": v(1.17, -1.03) * mm, "end": v(1.16, -0.97) * mm});
            skLineSegment(sketch, "E458", {"start": v(1.16, -0.97) * mm, "end": v(1.14, -0.92) * mm});
            skLineSegment(sketch, "E459", {"start": v(1.14, -0.92) * mm, "end": v(1.13, -0.86) * mm});
            skLineSegment(sketch, "E460", {"start": v(1.13, -0.86) * mm, "end": v(1.12, -0.8) * mm});
            skLineSegment(sketch, "E461", {"start": v(1.12, -0.8) * mm, "end": v(1.11, -0.74) * mm});
            skLineSegment(sketch, "E462", {"start": v(1.11, -0.74) * mm, "end": v(1.1, -0.68) * mm});
            skLineSegment(sketch, "E463", {"start": v(1.1, -0.68) * mm, "end": v(1.1, -0.61) * mm});
            skLineSegment(sketch, "E464", {"start": v(1.1, -0.61) * mm, "end": v(1.1, -0.56) * mm});
            skLineSegment(sketch, "E465", {"start": v(1.1, -0.56) * mm, "end": v(1.11, -0.5) * mm});
            skLineSegment(sketch, "E466", {"start": v(1.11, -0.5) * mm, "end": v(1.12, -0.44) * mm});
            skLineSegment(sketch, "E467", {"start": v(1.12, -0.44) * mm, "end": v(1.13, -0.38) * mm});
            skLineSegment(sketch, "E468", {"start": v(1.13, -0.38) * mm, "end": v(1.14, -0.33) * mm});
            skLineSegment(sketch, "E469", {"start": v(1.14, -0.33) * mm, "end": v(1.15, -0.27) * mm});
            skLineSegment(sketch, "E470", {"start": v(1.15, -0.27) * mm, "end": v(1.17, -0.22) * mm});
            skLineSegment(sketch, "E471", {"start": v(1.17, -0.22) * mm, "end": v(1.18, -0.16) * mm});
            skLineSegment(sketch, "E472", {"start": v(1.18, -0.16) * mm, "end": v(1.2, -0.1) * mm});
            skLineSegment(sketch, "E473", {"start": v(1.2, -0.1) * mm, "end": v(1.23, -0.06) * mm});
            skLineSegment(sketch, "E474", {"start": v(1.23, -0.06) * mm, "end": v(1.25, -0.01) * mm});
            skLineSegment(sketch, "E475", {"start": v(1.25, -0.01) * mm, "end": v(1.28, 0.03) * mm});
            skLineSegment(sketch, "E476", {"start": v(1.28, 0.03) * mm, "end": v(1.31, 0.08) * mm});
            skLineSegment(sketch, "E477", {"start": v(1.31, 0.08) * mm, "end": v(1.34, 0.12) * mm});
            skLineSegment(sketch, "E478", {"start": v(1.34, 0.12) * mm, "end": v(1.38, 0.16) * mm});
            skLineSegment(sketch, "E479", {"start": v(1.38, 0.16) * mm, "end": v(1.41, 0.2) * mm});
            skLineSegment(sketch, "E480", {"start": v(1.41, 0.2) * mm, "end": v(1.45, 0.24) * mm});
            skLineSegment(sketch, "E481", {"start": v(1.45, 0.24) * mm, "end": v(1.5, 0.27) * mm});
            skLineSegment(sketch, "E482", {"start": v(1.5, 0.27) * mm, "end": v(1.53, 0.3) * mm});
            skLineSegment(sketch, "E483", {"start": v(1.53, 0.3) * mm, "end": v(1.58, 0.34) * mm});
            skLineSegment(sketch, "E484", {"start": v(1.58, 0.34) * mm, "end": v(1.62, 0.37) * mm});
            skLineSegment(sketch, "E485", {"start": v(1.62, 0.37) * mm, "end": v(1.67, 0.4) * mm});
            skLineSegment(sketch, "E486", {"start": v(1.67, 0.4) * mm, "end": v(1.72, 0.42) * mm});
            skLineSegment(sketch, "E487", {"start": v(1.72, 0.42) * mm, "end": v(1.77, 0.44) * mm});
            skLineSegment(sketch, "E488", {"start": v(1.77, 0.44) * mm, "end": v(1.82, 0.46) * mm});
            skLineSegment(sketch, "E489", {"start": v(1.82, 0.46) * mm, "end": v(1.88, 0.48) * mm});
            skLineSegment(sketch, "E490", {"start": v(1.88, 0.48) * mm, "end": v(1.93, 0.5) * mm});
            skLineSegment(sketch, "E491", {"start": v(1.93, 0.5) * mm, "end": v(2, 0.51) * mm});
            skLineSegment(sketch, "E492", {"start": v(2, 0.51) * mm, "end": v(2.05, 0.52) * mm});
            skLineSegment(sketch, "E493", {"start": v(2.05, 0.52) * mm, "end": v(2.11, 0.53) * mm});
            skLineSegment(sketch, "E494", {"start": v(2.11, 0.53) * mm, "end": v(2.17, 0.53) * mm});
            skLineSegment(sketch, "E495", {"start": v(2.17, 0.53) * mm, "end": v(2.24, 0.53) * mm});
            skLineSegment(sketch, "E496", {"start": v(2.24, 0.53) * mm, "end": v(2.3, 0.53) * mm});
            skLineSegment(sketch, "E497", {"start": v(2.3, 0.53) * mm, "end": v(2.36, 0.53) * mm});
            skLineSegment(sketch, "E498", {"start": v(2.36, 0.53) * mm, "end": v(2.42, 0.52) * mm});
            skLineSegment(sketch, "E499", {"start": v(2.42, 0.52) * mm, "end": v(2.48, 0.51) * mm});
            skLineSegment(sketch, "E500", {"start": v(2.48, 0.51) * mm, "end": v(2.54, 0.5) * mm});
            skLineSegment(sketch, "E501", {"start": v(2.54, 0.5) * mm, "end": v(2.6, 0.48) * mm});
            skLineSegment(sketch, "E502", {"start": v(2.6, 0.48) * mm, "end": v(2.65, 0.46) * mm});
            skLineSegment(sketch, "E503", {"start": v(2.65, 0.46) * mm, "end": v(2.7, 0.44) * mm});
            skLineSegment(sketch, "E504", {"start": v(2.7, 0.44) * mm, "end": v(2.75, 0.42) * mm});
            skLineSegment(sketch, "E505", {"start": v(2.75, 0.42) * mm, "end": v(2.8, 0.4) * mm});
            skLineSegment(sketch, "E506", {"start": v(2.8, 0.4) * mm, "end": v(2.85, 0.37) * mm});
            skLineSegment(sketch, "E507", {"start": v(2.85, 0.37) * mm, "end": v(2.9, 0.34) * mm});
            skLineSegment(sketch, "E508", {"start": v(2.9, 0.34) * mm, "end": v(2.94, 0.3) * mm});
            skLineSegment(sketch, "E509", {"start": v(2.94, 0.3) * mm, "end": v(2.99, 0.27) * mm});
            skLineSegment(sketch, "E510", {"start": v(2.99, 0.27) * mm, "end": v(3.03, 0.23) * mm});
            skLineSegment(sketch, "E511", {"start": v(3.03, 0.23) * mm, "end": v(3.07, 0.2) * mm});
            skLineSegment(sketch, "E512", {"start": v(3.07, 0.2) * mm, "end": v(3.1, 0.16) * mm});
            skLineSegment(sketch, "E513", {"start": v(3.1, 0.16) * mm, "end": v(3.14, 0.11) * mm});
            skLineSegment(sketch, "E514", {"start": v(3.14, 0.11) * mm, "end": v(3.17, 0.07) * mm});
            skLineSegment(sketch, "E515", {"start": v(3.17, 0.07) * mm, "end": v(3.2, 0.03) * mm});
            skLineSegment(sketch, "E516", {"start": v(3.2, 0.03) * mm, "end": v(3.23, -0.02) * mm});
            skLineSegment(sketch, "E517", {"start": v(3.23, -0.02) * mm, "end": v(3.26, -0.07) * mm});
            skLineSegment(sketch, "E518", {"start": v(3.26, -0.07) * mm, "end": v(3.28, -0.12) * mm});
            skLineSegment(sketch, "E519", {"start": v(3.28, -0.12) * mm, "end": v(3.3, -0.17) * mm});
            skLineSegment(sketch, "E520", {"start": v(3.3, -0.17) * mm, "end": v(3.33, -0.23) * mm});
            skLineSegment(sketch, "E521", {"start": v(3.33, -0.23) * mm, "end": v(3.34, -0.28) * mm});
            skLineSegment(sketch, "E522", {"start": v(3.34, -0.28) * mm, "end": v(3.36, -0.34) * mm});
            skLineSegment(sketch, "E523", {"start": v(3.36, -0.34) * mm, "end": v(3.37, -0.4) * mm});
            skLineSegment(sketch, "E524", {"start": v(3.37, -0.4) * mm, "end": v(3.38, -0.46) * mm});
            skLineSegment(sketch, "E525", {"start": v(3.38, -0.46) * mm, "end": v(3.39, -0.52) * mm});
            skLineSegment(sketch, "E526", {"start": v(3.39, -0.52) * mm, "end": v(3.4, -0.58) * mm});
            skLineSegment(sketch, "E527", {"start": v(3.4, -0.58) * mm, "end": v(3.4, -0.65) * mm});
            skLineSegment(sketch, "E528", {"start": v(3.4, -0.65) * mm, "end": v(3.4, -0.7) * mm});
            skLineSegment(sketch, "E529", {"start": v(3.4, -0.7) * mm, "end": v(3.39, -0.76) * mm});
            skLineSegment(sketch, "E530", {"start": v(3.39, -0.76) * mm, "end": v(3.38, -0.82) * mm});
            skLineSegment(sketch, "E531", {"start": v(3.38, -0.82) * mm, "end": v(3.37, -0.88) * mm});
            skLineSegment(sketch, "E532", {"start": v(3.37, -0.88) * mm, "end": v(3.36, -0.93) * mm});
            skLineSegment(sketch, "E533", {"start": v(3.36, -0.93) * mm, "end": v(3.35, -0.99) * mm});
            skLineSegment(sketch, "E534", {"start": v(3.35, -0.99) * mm, "end": v(3.33, -1.04) * mm});
            skLineSegment(sketch, "E535", {"start": v(3.33, -1.04) * mm, "end": v(3.31, -1.1) * mm});
            skLineSegment(sketch, "E536", {"start": v(3.31, -1.1) * mm, "end": v(3.3, -1.14) * mm});
            skLineSegment(sketch, "E537", {"start": v(3.3, -1.14) * mm, "end": v(3.27, -1.2) * mm});
            skLineSegment(sketch, "E538", {"start": v(3.27, -1.2) * mm, "end": v(3.24, -1.24) * mm});
            skLineSegment(sketch, "E539", {"start": v(3.24, -1.24) * mm, "end": v(3.22, -1.29) * mm});
            skLineSegment(sketch, "E540", {"start": v(3.22, -1.29) * mm, "end": v(3.19, -1.33) * mm});
            skLineSegment(sketch, "E541", {"start": v(3.19, -1.33) * mm, "end": v(3.15, -1.38) * mm});
            skLineSegment(sketch, "E542", {"start": v(3.15, -1.38) * mm, "end": v(3.12, -1.42) * mm});
            skLineSegment(sketch, "E543", {"start": v(3.12, -1.42) * mm, "end": v(3.08, -1.46) * mm});
            skLineSegment(sketch, "E544", {"start": v(3.08, -1.46) * mm, "end": v(3.05, -1.5) * mm});
            skLineSegment(sketch, "E545", {"start": v(3.05, -1.5) * mm, "end": v(3, -1.53) * mm});
            skLineSegment(sketch, "E546", {"start": v(3, -1.53) * mm, "end": v(2.96, -1.56) * mm});
            skLineSegment(sketch, "E547", {"start": v(2.96, -1.56) * mm, "end": v(2.92, -1.6) * mm});
            skLineSegment(sketch, "E548", {"start": v(2.92, -1.6) * mm, "end": v(2.87, -1.63) * mm});
            skLineSegment(sketch, "E549", {"start": v(2.87, -1.63) * mm, "end": v(2.83, -1.65) * mm});
            skLineSegment(sketch, "E550", {"start": v(2.83, -1.65) * mm, "end": v(2.78, -1.68) * mm});
            skLineSegment(sketch, "E551", {"start": v(2.78, -1.68) * mm, "end": v(2.73, -1.7) * mm});
            skLineSegment(sketch, "E552", {"start": v(2.73, -1.7) * mm, "end": v(2.62, -1.74) * mm});
            skLineSegment(sketch, "E553", {"start": v(2.62, -1.74) * mm, "end": v(2.5, -1.77) * mm});
            skLineSegment(sketch, "E554", {"start": v(2.5, -1.77) * mm, "end": v(2.39, -1.79) * mm});
            skLineSegment(sketch, "E555", {"start": v(2.39, -1.79) * mm, "end": v(2.27, -1.8) * mm});
            skLineSegment(sketch, "E556", {"start": v(2.27, -1.8) * mm, "end": v(2.15, -1.79) * mm});
            skLineSegment(sketch, "E557", {"start": v(2.15, -1.79) * mm, "end": v(2.02, -1.77) * mm});
            skLineSegment(sketch, "E558", {"start": v(2.02, -1.77) * mm, "end": v(1.9, -1.74) * mm});
            skLineSegment(sketch, "E559", {"start": v(1.9, -1.74) * mm, "end": v(1.8, -1.7) * mm});
            skLineSegment(sketch, "E560", {"start": v(4.02, 1) * mm, "end": v(3.94, 1.08) * mm});
            skLineSegment(sketch, "E561", {"start": v(3.94, 1.08) * mm, "end": v(3.85, 1.15) * mm});
            skLineSegment(sketch, "E562", {"start": v(3.85, 1.15) * mm, "end": v(3.76, 1.22) * mm});
            skLineSegment(sketch, "E563", {"start": v(3.76, 1.22) * mm, "end": v(3.66, 1.28) * mm});
            skLineSegment(sketch, "E564", {"start": v(3.66, 1.28) * mm, "end": v(3.56, 1.34) * mm});
            skLineSegment(sketch, "E565", {"start": v(3.56, 1.34) * mm, "end": v(3.46, 1.4) * mm});
            skLineSegment(sketch, "E566", {"start": v(3.46, 1.4) * mm, "end": v(3.35, 1.45) * mm});
            skLineSegment(sketch, "E567", {"start": v(3.35, 1.45) * mm, "end": v(3.24, 1.5) * mm});
            skLineSegment(sketch, "E568", {"start": v(3.24, 1.5) * mm, "end": v(3, 1.57) * mm});
            skLineSegment(sketch, "E569", {"start": v(3, 1.57) * mm, "end": v(2.76, 1.63) * mm});
            skLineSegment(sketch, "E570", {"start": v(2.76, 1.63) * mm, "end": v(2.5, 1.66) * mm});
            skLineSegment(sketch, "E571", {"start": v(2.5, 1.66) * mm, "end": v(2.25, 1.67) * mm});
            skLineSegment(sketch, "E572", {"start": v(2.25, 1.67) * mm, "end": v(2, 1.66) * mm});
            skLineSegment(sketch, "E573", {"start": v(2, 1.66) * mm, "end": v(1.74, 1.63) * mm});
            skLineSegment(sketch, "E574", {"start": v(1.74, 1.63) * mm, "end": v(1.5, 1.57) * mm});
            skLineSegment(sketch, "E575", {"start": v(1.5, 1.57) * mm, "end": v(1.27, 1.49) * mm});
            skLineSegment(sketch, "E576", {"start": v(1.27, 1.49) * mm, "end": v(1.15, 1.44) * mm});
            skLineSegment(sketch, "E577", {"start": v(1.15, 1.44) * mm, "end": v(1.05, 1.39) * mm});
            skLineSegment(sketch, "E578", {"start": v(1.05, 1.39) * mm, "end": v(0.94, 1.33) * mm});
            skLineSegment(sketch, "E579", {"start": v(0.94, 1.33) * mm, "end": v(0.84, 1.27) * mm});
            skLineSegment(sketch, "E580", {"start": v(0.84, 1.27) * mm, "end": v(0.75, 1.2) * mm});
            skLineSegment(sketch, "E581", {"start": v(0.75, 1.2) * mm, "end": v(0.66, 1.14) * mm});
            skLineSegment(sketch, "E582", {"start": v(0.66, 1.14) * mm, "end": v(0.57, 1.07) * mm});
            skLineSegment(sketch, "E583", {"start": v(0.57, 1.07) * mm, "end": v(0.48, 1) * mm});
            skLineSegment(sketch, "E584", {"start": v(0.48, 1) * mm, "end": v(0.4, 0.91) * mm});
            skLineSegment(sketch, "E585", {"start": v(0.4, 0.91) * mm, "end": v(0.33, 0.83) * mm});
            skLineSegment(sketch, "E586", {"start": v(0.33, 0.83) * mm, "end": v(0.25, 0.74) * mm});
            skLineSegment(sketch, "E587", {"start": v(0.25, 0.74) * mm, "end": v(0.19, 0.65) * mm});
            skLineSegment(sketch, "E588", {"start": v(0.19, 0.65) * mm, "end": v(0.12, 0.56) * mm});
            skLineSegment(sketch, "E589", {"start": v(0.12, 0.56) * mm, "end": v(0.07, 0.47) * mm});
            skLineSegment(sketch, "E590", {"start": v(0.07, 0.47) * mm, "end": v(0.01, 0.37) * mm});
            skLineSegment(sketch, "E591", {"start": v(0.01, 0.37) * mm, "end": v(-0.04, 0.26) * mm});
            skLineSegment(sketch, "E592", {"start": v(-0.04, 0.26) * mm, "end": v(-0.08, 0.16) * mm});
            skLineSegment(sketch, "E593", {"start": v(-0.08, 0.16) * mm, "end": v(-0.12, 0.05) * mm});
            skLineSegment(sketch, "E594", {"start": v(-0.12, 0.05) * mm, "end": v(-0.15, -0.06) * mm});
            skLineSegment(sketch, "E595", {"start": v(-0.15, -0.06) * mm, "end": v(-0.18, -0.17) * mm});
            skLineSegment(sketch, "E596", {"start": v(-0.18, -0.17) * mm, "end": v(-0.2, -0.29) * mm});
            skLineSegment(sketch, "E597", {"start": v(-0.2, -0.29) * mm, "end": v(-0.21, -0.4) * mm});
            skLineSegment(sketch, "E598", {"start": v(-0.21, -0.4) * mm, "end": v(-0.22, -0.52) * mm});
            skLineSegment(sketch, "E599", {"start": v(-0.22, -0.52) * mm, "end": v(-0.23, -0.65) * mm});
            skLineSegment(sketch, "E600", {"start": v(-0.23, -0.65) * mm, "end": v(-0.22, -0.76) * mm});
            skLineSegment(sketch, "E601", {"start": v(-0.22, -0.76) * mm, "end": v(-0.21, -0.88) * mm});
            skLineSegment(sketch, "E602", {"start": v(-0.21, -0.88) * mm, "end": v(-0.2, -0.99) * mm});
            skLineSegment(sketch, "E603", {"start": v(-0.2, -0.99) * mm, "end": v(-0.18, -1.1) * mm});
            skLineSegment(sketch, "E604", {"start": v(-0.18, -1.1) * mm, "end": v(-0.15, -1.2) * mm});
            skLineSegment(sketch, "E605", {"start": v(-0.15, -1.2) * mm, "end": v(-0.12, -1.32) * mm});
            skLineSegment(sketch, "E606", {"start": v(-0.12, -1.32) * mm, "end": v(-0.08, -1.42) * mm});
            skLineSegment(sketch, "E607", {"start": v(-0.08, -1.42) * mm, "end": v(-0.04, -1.53) * mm});
            skLineSegment(sketch, "E608", {"start": v(-0.04, -1.53) * mm, "end": v(0, -1.63) * mm});
            skLineSegment(sketch, "E609", {"start": v(0, -1.63) * mm, "end": v(0.06, -1.73) * mm});
            skLineSegment(sketch, "E610", {"start": v(0.06, -1.73) * mm, "end": v(0.12, -1.83) * mm});
            skLineSegment(sketch, "E611", {"start": v(0.12, -1.83) * mm, "end": v(0.18, -1.92) * mm});
            skLineSegment(sketch, "E612", {"start": v(0.18, -1.92) * mm, "end": v(0.25, -2) * mm});
            skLineSegment(sketch, "E613", {"start": v(0.25, -2) * mm, "end": v(0.32, -2.1) * mm});
            skLineSegment(sketch, "E614", {"start": v(0.32, -2.1) * mm, "end": v(0.4, -2.18) * mm});
            skLineSegment(sketch, "E615", {"start": v(0.4, -2.18) * mm, "end": v(0.47, -2.26) * mm});
            skLineSegment(sketch, "E616", {"start": v(0.47, -2.26) * mm, "end": v(0.56, -2.33) * mm});
            skLineSegment(sketch, "E617", {"start": v(0.56, -2.33) * mm, "end": v(0.65, -2.4) * mm});
            skLineSegment(sketch, "E618", {"start": v(0.65, -2.4) * mm, "end": v(0.74, -2.47) * mm});
            skLineSegment(sketch, "E619", {"start": v(0.74, -2.47) * mm, "end": v(0.84, -2.53) * mm});
            skLineSegment(sketch, "E620", {"start": v(0.84, -2.53) * mm, "end": v(0.94, -2.6) * mm});
            skLineSegment(sketch, "E621", {"start": v(0.94, -2.6) * mm, "end": v(1.04, -2.65) * mm});
            skLineSegment(sketch, "E622", {"start": v(1.04, -2.65) * mm, "end": v(1.15, -2.7) * mm});
            skLineSegment(sketch, "E623", {"start": v(1.15, -2.7) * mm, "end": v(1.26, -2.75) * mm});
            skLineSegment(sketch, "E624", {"start": v(1.26, -2.75) * mm, "end": v(1.37, -2.79) * mm});
            skLineSegment(sketch, "E625", {"start": v(1.37, -2.79) * mm, "end": v(1.49, -2.82) * mm});
            skLineSegment(sketch, "E626", {"start": v(1.49, -2.82) * mm, "end": v(1.6, -2.85) * mm});
            skLineSegment(sketch, "E627", {"start": v(1.6, -2.85) * mm, "end": v(1.73, -2.88) * mm});
            skLineSegment(sketch, "E628", {"start": v(1.73, -2.88) * mm, "end": v(1.85, -2.9) * mm});
            skLineSegment(sketch, "E629", {"start": v(1.85, -2.9) * mm, "end": v(1.98, -2.91) * mm});
            skLineSegment(sketch, "E630", {"start": v(1.98, -2.91) * mm, "end": v(2.1, -2.92) * mm});
            skLineSegment(sketch, "E631", {"start": v(2.1, -2.92) * mm, "end": v(2.24, -2.92) * mm});
            skLineSegment(sketch, "E632", {"start": v(2.24, -2.92) * mm, "end": v(2.37, -2.92) * mm});
            skLineSegment(sketch, "E633", {"start": v(2.37, -2.92) * mm, "end": v(2.5, -2.91) * mm});
            skLineSegment(sketch, "E634", {"start": v(2.5, -2.91) * mm, "end": v(2.63, -2.9) * mm});
            skLineSegment(sketch, "E635", {"start": v(2.63, -2.9) * mm, "end": v(2.75, -2.88) * mm});
            skLineSegment(sketch, "E636", {"start": v(2.75, -2.88) * mm, "end": v(2.87, -2.85) * mm});
            skLineSegment(sketch, "E637", {"start": v(2.87, -2.85) * mm, "end": v(3, -2.82) * mm});
            skLineSegment(sketch, "E638", {"start": v(3, -2.82) * mm, "end": v(3.11, -2.78) * mm});
            skLineSegment(sketch, "E639", {"start": v(3.11, -2.78) * mm, "end": v(3.23, -2.74) * mm});
            skLineSegment(sketch, "E640", {"start": v(3.23, -2.74) * mm, "end": v(3.34, -2.7) * mm});
            skLineSegment(sketch, "E641", {"start": v(3.34, -2.7) * mm, "end": v(3.45, -2.64) * mm});
            skLineSegment(sketch, "E642", {"start": v(3.45, -2.64) * mm, "end": v(3.55, -2.58) * mm});
            skLineSegment(sketch, "E643", {"start": v(3.55, -2.58) * mm, "end": v(3.65, -2.52) * mm});
            skLineSegment(sketch, "E644", {"start": v(3.65, -2.52) * mm, "end": v(3.75, -2.46) * mm});
            skLineSegment(sketch, "E645", {"start": v(3.75, -2.46) * mm, "end": v(3.84, -2.4) * mm});
            skLineSegment(sketch, "E646", {"start": v(3.84, -2.4) * mm, "end": v(3.93, -2.32) * mm});
            skLineSegment(sketch, "E647", {"start": v(3.93, -2.32) * mm, "end": v(4.02, -2.24) * mm});
            skLineSegment(sketch, "E648", {"start": v(4.02, -2.24) * mm, "end": v(4.1, -2.16) * mm});
            skLineSegment(sketch, "E649", {"start": v(4.1, -2.16) * mm, "end": v(4.17, -2.08) * mm});
            skLineSegment(sketch, "E650", {"start": v(4.17, -2.08) * mm, "end": v(4.24, -2) * mm});
            skLineSegment(sketch, "E651", {"start": v(4.24, -2) * mm, "end": v(4.31, -1.9) * mm});
            skLineSegment(sketch, "E652", {"start": v(4.31, -1.9) * mm, "end": v(4.37, -1.81) * mm});
            skLineSegment(sketch, "E653", {"start": v(4.37, -1.81) * mm, "end": v(4.43, -1.72) * mm});
            skLineSegment(sketch, "E654", {"start": v(4.43, -1.72) * mm, "end": v(4.49, -1.62) * mm});
            skLineSegment(sketch, "E655", {"start": v(4.49, -1.62) * mm, "end": v(4.54, -1.52) * mm});
            skLineSegment(sketch, "E656", {"start": v(4.54, -1.52) * mm, "end": v(4.58, -1.41) * mm});
            skLineSegment(sketch, "E657", {"start": v(4.58, -1.41) * mm, "end": v(4.62, -1.3) * mm});
            skLineSegment(sketch, "E658", {"start": v(4.62, -1.3) * mm, "end": v(4.65, -1.2) * mm});
            skLineSegment(sketch, "E659", {"start": v(4.65, -1.2) * mm, "end": v(4.68, -1.08) * mm});
            skLineSegment(sketch, "E660", {"start": v(4.68, -1.08) * mm, "end": v(4.7, -0.97) * mm});
            skLineSegment(sketch, "E661", {"start": v(4.7, -0.97) * mm, "end": v(4.71, -0.85) * mm});
            skLineSegment(sketch, "E662", {"start": v(4.71, -0.85) * mm, "end": v(4.72, -0.73) * mm});
            skLineSegment(sketch, "E663", {"start": v(4.72, -0.73) * mm, "end": v(4.72, -0.61) * mm});
            skLineSegment(sketch, "E664", {"start": v(4.72, -0.61) * mm, "end": v(4.72, -0.5) * mm});
            skLineSegment(sketch, "E665", {"start": v(4.72, -0.5) * mm, "end": v(4.71, -0.38) * mm});
            skLineSegment(sketch, "E666", {"start": v(4.71, -0.38) * mm, "end": v(4.7, -0.27) * mm});
            skLineSegment(sketch, "E667", {"start": v(4.7, -0.27) * mm, "end": v(4.68, -0.15) * mm});
            skLineSegment(sketch, "E668", {"start": v(4.68, -0.15) * mm, "end": v(4.65, -0.04) * mm});
            skLineSegment(sketch, "E669", {"start": v(4.65, -0.04) * mm, "end": v(4.62, 0.06) * mm});
            skLineSegment(sketch, "E670", {"start": v(4.62, 0.06) * mm, "end": v(4.58, 0.17) * mm});
            skLineSegment(sketch, "E671", {"start": v(4.58, 0.17) * mm, "end": v(4.54, 0.28) * mm});
            skLineSegment(sketch, "E672", {"start": v(4.54, 0.28) * mm, "end": v(4.5, 0.38) * mm});
            skLineSegment(sketch, "E673", {"start": v(4.5, 0.38) * mm, "end": v(4.44, 0.47) * mm});
            skLineSegment(sketch, "E674", {"start": v(4.44, 0.47) * mm, "end": v(4.38, 0.57) * mm});
            skLineSegment(sketch, "E675", {"start": v(4.38, 0.57) * mm, "end": v(4.32, 0.66) * mm});
            skLineSegment(sketch, "E676", {"start": v(4.32, 0.66) * mm, "end": v(4.25, 0.75) * mm});
            skLineSegment(sketch, "E677", {"start": v(4.25, 0.75) * mm, "end": v(4.18, 0.84) * mm});
            skLineSegment(sketch, "E678", {"start": v(4.18, 0.84) * mm, "end": v(4.1, 0.92) * mm});
            skLineSegment(sketch, "E679", {"start": v(4.1, 0.92) * mm, "end": v(4.02, 1) * mm});
            skLineSegment(sketch, "E680", {"start": v(7.4, -1.13) * mm, "end": v(7.26, -0.79) * mm});
            skLineSegment(sketch, "E681", {"start": v(7.26, -0.79) * mm, "end": v(7.13, -0.45) * mm});
            skLineSegment(sketch, "E682", {"start": v(7.13, -0.45) * mm, "end": v(7, -0.1) * mm});
            skLineSegment(sketch, "E683", {"start": v(7, -0.1) * mm, "end": v(6.87, 0.23) * mm});
            skLineSegment(sketch, "E684", {"start": v(6.87, 0.23) * mm, "end": v(6.73, 0.57) * mm});
            skLineSegment(sketch, "E685", {"start": v(6.73, 0.57) * mm, "end": v(6.6, 0.9) * mm});
            skLineSegment(sketch, "E686", {"start": v(6.6, 0.9) * mm, "end": v(6.47, 1.25) * mm});
            skLineSegment(sketch, "E687", {"start": v(6.47, 1.25) * mm, "end": v(6.34, 1.59) * mm});
            skLineSegment(sketch, "E688", {"start": v(6.34, 1.59) * mm, "end": v(6.16, 1.59) * mm});
            skLineSegment(sketch, "E689", {"start": v(6.16, 1.59) * mm, "end": v(5.98, 1.59) * mm});
            skLineSegment(sketch, "E690", {"start": v(5.98, 1.59) * mm, "end": v(5.8, 1.59) * mm});
            skLineSegment(sketch, "E691", {"start": v(5.8, 1.59) * mm, "end": v(5.63, 1.59) * mm});
            skLineSegment(sketch, "E692", {"start": v(5.63, 1.59) * mm, "end": v(5.45, 1.59) * mm});
            skLineSegment(sketch, "E693", {"start": v(5.45, 1.59) * mm, "end": v(5.27, 1.59) * mm});
            skLineSegment(sketch, "E694", {"start": v(5.27, 1.59) * mm, "end": v(5.1, 1.59) * mm});
            skLineSegment(sketch, "E695", {"start": v(5.1, 1.59) * mm, "end": v(4.91, 1.59) * mm});
            skLineSegment(sketch, "E696", {"start": v(4.91, 1.59) * mm, "end": v(5.15, 1.03) * mm});
            skLineSegment(sketch, "E697", {"start": v(5.15, 1.03) * mm, "end": v(5.4, 0.48) * mm});
            skLineSegment(sketch, "E698", {"start": v(5.4, 0.48) * mm, "end": v(5.63, -0.08) * mm});
            skLineSegment(sketch, "E699", {"start": v(5.63, -0.08) * mm, "end": v(5.87, -0.64) * mm});
            skLineSegment(sketch, "E700", {"start": v(5.87, -0.64) * mm, "end": v(6.11, -1.2) * mm});
            skLineSegment(sketch, "E701", {"start": v(6.11, -1.2) * mm, "end": v(6.35, -1.75) * mm});
            skLineSegment(sketch, "E702", {"start": v(6.35, -1.75) * mm, "end": v(6.59, -2.3) * mm});
            skLineSegment(sketch, "E703", {"start": v(6.59, -2.3) * mm, "end": v(6.83, -2.86) * mm});
            skLineSegment(sketch, "E704", {"start": v(6.83, -2.86) * mm, "end": v(6.97, -2.86) * mm});
            skLineSegment(sketch, "E705", {"start": v(6.97, -2.86) * mm, "end": v(7.1, -2.86) * mm});
            skLineSegment(sketch, "E706", {"start": v(7.1, -2.86) * mm, "end": v(7.25, -2.86) * mm});
            skLineSegment(sketch, "E707", {"start": v(7.25, -2.86) * mm, "end": v(7.39, -2.86) * mm});
            skLineSegment(sketch, "E708", {"start": v(7.39, -2.86) * mm, "end": v(7.53, -2.86) * mm});
            skLineSegment(sketch, "E709", {"start": v(7.53, -2.86) * mm, "end": v(7.67, -2.86) * mm});
            skLineSegment(sketch, "E710", {"start": v(7.67, -2.86) * mm, "end": v(7.8, -2.86) * mm});
            skLineSegment(sketch, "E711", {"start": v(7.8, -2.86) * mm, "end": v(7.95, -2.86) * mm});
            skLineSegment(sketch, "E712", {"start": v(7.95, -2.86) * mm, "end": v(8.18, -2.3) * mm});
            skLineSegment(sketch, "E713", {"start": v(8.18, -2.3) * mm, "end": v(8.42, -1.75) * mm});
            skLineSegment(sketch, "E714", {"start": v(8.42, -1.75) * mm, "end": v(8.66, -1.2) * mm});
            skLineSegment(sketch, "E715", {"start": v(8.66, -1.2) * mm, "end": v(8.9, -0.64) * mm});
            skLineSegment(sketch, "E716", {"start": v(8.9, -0.64) * mm, "end": v(9.14, -0.08) * mm});
            skLineSegment(sketch, "E717", {"start": v(9.14, -0.08) * mm, "end": v(9.38, 0.48) * mm});
            skLineSegment(sketch, "E718", {"start": v(9.38, 0.48) * mm, "end": v(9.61, 1.03) * mm});
            skLineSegment(sketch, "E719", {"start": v(9.61, 1.03) * mm, "end": v(9.85, 1.59) * mm});
            skLineSegment(sketch, "E720", {"start": v(9.85, 1.59) * mm, "end": v(9.68, 1.59) * mm});
            skLineSegment(sketch, "E721", {"start": v(9.68, 1.59) * mm, "end": v(9.5, 1.59) * mm});
            skLineSegment(sketch, "E722", {"start": v(9.5, 1.59) * mm, "end": v(9.33, 1.59) * mm});
            skLineSegment(sketch, "E723", {"start": v(9.33, 1.59) * mm, "end": v(9.15, 1.59) * mm});
            skLineSegment(sketch, "E724", {"start": v(9.15, 1.59) * mm, "end": v(8.98, 1.59) * mm});
            skLineSegment(sketch, "E725", {"start": v(8.98, 1.59) * mm, "end": v(8.8, 1.59) * mm});
            skLineSegment(sketch, "E726", {"start": v(8.8, 1.59) * mm, "end": v(8.62, 1.59) * mm});
            skLineSegment(sketch, "E727", {"start": v(8.62, 1.59) * mm, "end": v(8.45, 1.59) * mm});
            skLineSegment(sketch, "E728", {"start": v(8.45, 1.59) * mm, "end": v(8.32, 1.25) * mm});
            skLineSegment(sketch, "E729", {"start": v(8.32, 1.25) * mm, "end": v(8.18, 0.9) * mm});
            skLineSegment(sketch, "E730", {"start": v(8.18, 0.9) * mm, "end": v(8.05, 0.57) * mm});
            skLineSegment(sketch, "E731", {"start": v(8.05, 0.57) * mm, "end": v(7.92, 0.23) * mm});
            skLineSegment(sketch, "E732", {"start": v(7.92, 0.23) * mm, "end": v(7.79, -0.1) * mm});
            skLineSegment(sketch, "E733", {"start": v(7.79, -0.1) * mm, "end": v(7.66, -0.45) * mm});
            skLineSegment(sketch, "E734", {"start": v(7.66, -0.45) * mm, "end": v(7.52, -0.79) * mm});
            skLineSegment(sketch, "E735", {"start": v(7.52, -0.79) * mm, "end": v(7.4, -1.13) * mm});
            skLineSegment(sketch, "E736", {"start": v(12.07, -1.7) * mm, "end": v(12.02, -1.68) * mm});
            skLineSegment(sketch, "E737", {"start": v(12.02, -1.68) * mm, "end": v(11.97, -1.65) * mm});
            skLineSegment(sketch, "E738", {"start": v(11.97, -1.65) * mm, "end": v(11.92, -1.62) * mm});
            skLineSegment(sketch, "E739", {"start": v(11.92, -1.62) * mm, "end": v(11.88, -1.6) * mm});
            skLineSegment(sketch, "E740", {"start": v(11.88, -1.6) * mm, "end": v(11.83, -1.56) * mm});
            skLineSegment(sketch, "E741", {"start": v(11.83, -1.56) * mm, "end": v(11.79, -1.53) * mm});
            skLineSegment(sketch, "E742", {"start": v(11.79, -1.53) * mm, "end": v(11.75, -1.5) * mm});
            skLineSegment(sketch, "E743", {"start": v(11.75, -1.5) * mm, "end": v(11.7, -1.45) * mm});
            skLineSegment(sketch, "E744", {"start": v(11.7, -1.45) * mm, "end": v(11.67, -1.41) * mm});
            skLineSegment(sketch, "E745", {"start": v(11.67, -1.41) * mm, "end": v(11.64, -1.37) * mm});
            skLineSegment(sketch, "E746", {"start": v(11.64, -1.37) * mm, "end": v(11.6, -1.32) * mm});
            skLineSegment(sketch, "E747", {"start": v(11.6, -1.32) * mm, "end": v(11.57, -1.28) * mm});
            skLineSegment(sketch, "E748", {"start": v(11.57, -1.28) * mm, "end": v(11.54, -1.23) * mm});
            skLineSegment(sketch, "E749", {"start": v(11.54, -1.23) * mm, "end": v(11.52, -1.18) * mm});
            skLineSegment(sketch, "E750", {"start": v(11.52, -1.18) * mm, "end": v(11.5, -1.13) * mm});
            skLineSegment(sketch, "E751", {"start": v(11.5, -1.13) * mm, "end": v(11.47, -1.08) * mm});
            skLineSegment(sketch, "E752", {"start": v(11.47, -1.08) * mm, "end": v(11.45, -1.03) * mm});
            skLineSegment(sketch, "E753", {"start": v(11.45, -1.03) * mm, "end": v(11.43, -0.97) * mm});
            skLineSegment(sketch, "E754", {"start": v(11.43, -0.97) * mm, "end": v(11.42, -0.92) * mm});
            skLineSegment(sketch, "E755", {"start": v(11.42, -0.92) * mm, "end": v(11.4, -0.86) * mm});
            skLineSegment(sketch, "E756", {"start": v(11.4, -0.86) * mm, "end": v(11.4, -0.8) * mm});
            skLineSegment(sketch, "E757", {"start": v(11.4, -0.8) * mm, "end": v(11.39, -0.74) * mm});
            skLineSegment(sketch, "E758", {"start": v(11.39, -0.74) * mm, "end": v(11.38, -0.68) * mm});
            skLineSegment(sketch, "E759", {"start": v(11.38, -0.68) * mm, "end": v(11.38, -0.61) * mm});
            skLineSegment(sketch, "E760", {"start": v(11.38, -0.61) * mm, "end": v(11.38, -0.56) * mm});
            skLineSegment(sketch, "E761", {"start": v(11.38, -0.56) * mm, "end": v(11.39, -0.5) * mm});
            skLineSegment(sketch, "E762", {"start": v(11.39, -0.5) * mm, "end": v(11.4, -0.44) * mm});
            skLineSegment(sketch, "E763", {"start": v(11.4, -0.44) * mm, "end": v(11.4, -0.38) * mm});
            skLineSegment(sketch, "E764", {"start": v(11.4, -0.38) * mm, "end": v(11.41, -0.33) * mm});
            skLineSegment(sketch, "E765", {"start": v(11.41, -0.33) * mm, "end": v(11.43, -0.27) * mm});
            skLineSegment(sketch, "E766", {"start": v(11.43, -0.27) * mm, "end": v(11.44, -0.22) * mm});
            skLineSegment(sketch, "E767", {"start": v(11.44, -0.22) * mm, "end": v(11.46, -0.16) * mm});
            skLineSegment(sketch, "E768", {"start": v(11.46, -0.16) * mm, "end": v(11.48, -0.1) * mm});
            skLineSegment(sketch, "E769", {"start": v(11.48, -0.1) * mm, "end": v(11.5, -0.06) * mm});
            skLineSegment(sketch, "E770", {"start": v(11.5, -0.06) * mm, "end": v(11.53, -0.01) * mm});
            skLineSegment(sketch, "E771", {"start": v(11.53, -0.01) * mm, "end": v(11.56, 0.03) * mm});
            skLineSegment(sketch, "E772", {"start": v(11.56, 0.03) * mm, "end": v(11.59, 0.08) * mm});
            skLineSegment(sketch, "E773", {"start": v(11.59, 0.08) * mm, "end": v(11.62, 0.12) * mm});
            skLineSegment(sketch, "E774", {"start": v(11.62, 0.12) * mm, "end": v(11.65, 0.16) * mm});
            skLineSegment(sketch, "E775", {"start": v(11.65, 0.16) * mm, "end": v(11.69, 0.2) * mm});
            skLineSegment(sketch, "E776", {"start": v(11.69, 0.2) * mm, "end": v(11.73, 0.24) * mm});
            skLineSegment(sketch, "E777", {"start": v(11.73, 0.24) * mm, "end": v(11.77, 0.27) * mm});
            skLineSegment(sketch, "E778", {"start": v(11.77, 0.27) * mm, "end": v(11.8, 0.3) * mm});
            skLineSegment(sketch, "E779", {"start": v(11.8, 0.3) * mm, "end": v(11.85, 0.34) * mm});
            skLineSegment(sketch, "E780", {"start": v(11.85, 0.34) * mm, "end": v(11.9, 0.37) * mm});
            skLineSegment(sketch, "E781", {"start": v(11.9, 0.37) * mm, "end": v(11.95, 0.4) * mm});
            skLineSegment(sketch, "E782", {"start": v(11.95, 0.4) * mm, "end": v(12, 0.42) * mm});
            skLineSegment(sketch, "E783", {"start": v(12, 0.42) * mm, "end": v(12.05, 0.44) * mm});
            skLineSegment(sketch, "E784", {"start": v(12.05, 0.44) * mm, "end": v(12.1, 0.46) * mm});
            skLineSegment(sketch, "E785", {"start": v(12.1, 0.46) * mm, "end": v(12.15, 0.48) * mm});
            skLineSegment(sketch, "E786", {"start": v(12.15, 0.48) * mm, "end": v(12.21, 0.5) * mm});
            skLineSegment(sketch, "E787", {"start": v(12.21, 0.5) * mm, "end": v(12.27, 0.51) * mm});
            skLineSegment(sketch, "E788", {"start": v(12.27, 0.51) * mm, "end": v(12.33, 0.52) * mm});
            skLineSegment(sketch, "E789", {"start": v(12.33, 0.52) * mm, "end": v(12.39, 0.53) * mm});
            skLineSegment(sketch, "E790", {"start": v(12.39, 0.53) * mm, "end": v(12.45, 0.53) * mm});
            skLineSegment(sketch, "E791", {"start": v(12.45, 0.53) * mm, "end": v(12.51, 0.53) * mm});
            skLineSegment(sketch, "E792", {"start": v(12.51, 0.53) * mm, "end": v(12.58, 0.53) * mm});
            skLineSegment(sketch, "E793", {"start": v(12.58, 0.53) * mm, "end": v(12.64, 0.53) * mm});
            skLineSegment(sketch, "E794", {"start": v(12.64, 0.53) * mm, "end": v(12.7, 0.52) * mm});
            skLineSegment(sketch, "E795", {"start": v(12.7, 0.52) * mm, "end": v(12.76, 0.51) * mm});
            skLineSegment(sketch, "E796", {"start": v(12.76, 0.51) * mm, "end": v(12.82, 0.5) * mm});
            skLineSegment(sketch, "E797", {"start": v(12.82, 0.5) * mm, "end": v(12.87, 0.48) * mm});
            skLineSegment(sketch, "E798", {"start": v(12.87, 0.48) * mm, "end": v(12.93, 0.46) * mm});
            skLineSegment(sketch, "E799", {"start": v(12.93, 0.46) * mm, "end": v(12.98, 0.44) * mm});
            skLineSegment(sketch, "E800", {"start": v(12.98, 0.44) * mm, "end": v(13.03, 0.42) * mm});
            skLineSegment(sketch, "E801", {"start": v(13.03, 0.42) * mm, "end": v(13.08, 0.4) * mm});
            skLineSegment(sketch, "E802", {"start": v(13.08, 0.4) * mm, "end": v(13.13, 0.37) * mm});
            skLineSegment(sketch, "E803", {"start": v(13.13, 0.37) * mm, "end": v(13.17, 0.34) * mm});
            skLineSegment(sketch, "E804", {"start": v(13.17, 0.34) * mm, "end": v(13.22, 0.3) * mm});
            skLineSegment(sketch, "E805", {"start": v(13.22, 0.3) * mm, "end": v(13.26, 0.27) * mm});
            skLineSegment(sketch, "E806", {"start": v(13.26, 0.27) * mm, "end": v(13.3, 0.23) * mm});
            skLineSegment(sketch, "E807", {"start": v(13.3, 0.23) * mm, "end": v(13.34, 0.2) * mm});
            skLineSegment(sketch, "E808", {"start": v(13.34, 0.2) * mm, "end": v(13.38, 0.16) * mm});
            skLineSegment(sketch, "E809", {"start": v(13.38, 0.16) * mm, "end": v(13.41, 0.11) * mm});
            skLineSegment(sketch, "E810", {"start": v(13.41, 0.11) * mm, "end": v(13.45, 0.07) * mm});
            skLineSegment(sketch, "E811", {"start": v(13.45, 0.07) * mm, "end": v(13.48, 0.03) * mm});
            skLineSegment(sketch, "E812", {"start": v(13.48, 0.03) * mm, "end": v(13.5, -0.02) * mm});
            skLineSegment(sketch, "E813", {"start": v(13.5, -0.02) * mm, "end": v(13.53, -0.07) * mm});
            skLineSegment(sketch, "E814", {"start": v(13.53, -0.07) * mm, "end": v(13.56, -0.12) * mm});
            skLineSegment(sketch, "E815", {"start": v(13.56, -0.12) * mm, "end": v(13.58, -0.17) * mm});
            skLineSegment(sketch, "E816", {"start": v(13.58, -0.17) * mm, "end": v(13.6, -0.23) * mm});
            skLineSegment(sketch, "E817", {"start": v(13.6, -0.23) * mm, "end": v(13.62, -0.28) * mm});
            skLineSegment(sketch, "E818", {"start": v(13.62, -0.28) * mm, "end": v(13.63, -0.34) * mm});
            skLineSegment(sketch, "E819", {"start": v(13.63, -0.34) * mm, "end": v(13.65, -0.4) * mm});
            skLineSegment(sketch, "E820", {"start": v(13.65, -0.4) * mm, "end": v(13.66, -0.46) * mm});
            skLineSegment(sketch, "E821", {"start": v(13.66, -0.46) * mm, "end": v(13.66, -0.52) * mm});
            skLineSegment(sketch, "E822", {"start": v(13.66, -0.52) * mm, "end": v(13.67, -0.58) * mm});
            skLineSegment(sketch, "E823", {"start": v(13.67, -0.58) * mm, "end": v(13.67, -0.65) * mm});
            skLineSegment(sketch, "E824", {"start": v(13.67, -0.65) * mm, "end": v(13.67, -0.7) * mm});
            skLineSegment(sketch, "E825", {"start": v(13.67, -0.7) * mm, "end": v(13.66, -0.76) * mm});
            skLineSegment(sketch, "E826", {"start": v(13.66, -0.76) * mm, "end": v(13.66, -0.82) * mm});
            skLineSegment(sketch, "E827", {"start": v(13.66, -0.82) * mm, "end": v(13.65, -0.87) * mm});
            skLineSegment(sketch, "E828", {"start": v(13.65, -0.87) * mm, "end": v(13.64, -0.93) * mm});
            skLineSegment(sketch, "E829", {"start": v(13.64, -0.93) * mm, "end": v(13.62, -0.99) * mm});
            skLineSegment(sketch, "E830", {"start": v(13.62, -0.99) * mm, "end": v(13.6, -1.04) * mm});
            skLineSegment(sketch, "E831", {"start": v(13.6, -1.04) * mm, "end": v(13.59, -1.1) * mm});
            skLineSegment(sketch, "E832", {"start": v(13.59, -1.1) * mm, "end": v(13.57, -1.14) * mm});
            skLineSegment(sketch, "E833", {"start": v(13.57, -1.14) * mm, "end": v(13.54, -1.2) * mm});
            skLineSegment(sketch, "E834", {"start": v(13.54, -1.2) * mm, "end": v(13.52, -1.24) * mm});
            skLineSegment(sketch, "E835", {"start": v(13.52, -1.24) * mm, "end": v(13.5, -1.29) * mm});
            skLineSegment(sketch, "E836", {"start": v(13.5, -1.29) * mm, "end": v(13.46, -1.33) * mm});
            skLineSegment(sketch, "E837", {"start": v(13.46, -1.33) * mm, "end": v(13.43, -1.38) * mm});
            skLineSegment(sketch, "E838", {"start": v(13.43, -1.38) * mm, "end": v(13.4, -1.42) * mm});
            skLineSegment(sketch, "E839", {"start": v(13.4, -1.42) * mm, "end": v(13.36, -1.46) * mm});
            skLineSegment(sketch, "E840", {"start": v(13.36, -1.46) * mm, "end": v(13.32, -1.5) * mm});
            skLineSegment(sketch, "E841", {"start": v(13.32, -1.5) * mm, "end": v(13.28, -1.53) * mm});
            skLineSegment(sketch, "E842", {"start": v(13.28, -1.53) * mm, "end": v(13.24, -1.56) * mm});
            skLineSegment(sketch, "E843", {"start": v(13.24, -1.56) * mm, "end": v(13.2, -1.6) * mm});
            skLineSegment(sketch, "E844", {"start": v(13.2, -1.6) * mm, "end": v(13.15, -1.62) * mm});
            skLineSegment(sketch, "E845", {"start": v(13.15, -1.62) * mm, "end": v(13.1, -1.65) * mm});
            skLineSegment(sketch, "E846", {"start": v(13.1, -1.65) * mm, "end": v(13.05, -1.68) * mm});
            skLineSegment(sketch, "E847", {"start": v(13.05, -1.68) * mm, "end": v(13, -1.7) * mm});
            skLineSegment(sketch, "E848", {"start": v(13, -1.7) * mm, "end": v(12.9, -1.74) * mm});
            skLineSegment(sketch, "E849", {"start": v(12.9, -1.74) * mm, "end": v(12.78, -1.77) * mm});
            skLineSegment(sketch, "E850", {"start": v(12.78, -1.77) * mm, "end": v(12.67, -1.79) * mm});
            skLineSegment(sketch, "E851", {"start": v(12.67, -1.79) * mm, "end": v(12.54, -1.8) * mm});
            skLineSegment(sketch, "E852", {"start": v(12.54, -1.8) * mm, "end": v(12.42, -1.79) * mm});
            skLineSegment(sketch, "E853", {"start": v(12.42, -1.79) * mm, "end": v(12.3, -1.77) * mm});
            skLineSegment(sketch, "E854", {"start": v(12.3, -1.77) * mm, "end": v(12.18, -1.74) * mm});
            skLineSegment(sketch, "E855", {"start": v(12.18, -1.74) * mm, "end": v(12.07, -1.7) * mm});
            skLineSegment(sketch, "E856", {"start": v(14.82, 0.28) * mm, "end": v(14.77, 0.38) * mm});
            skLineSegment(sketch, "E857", {"start": v(14.77, 0.38) * mm, "end": v(14.72, 0.47) * mm});
            skLineSegment(sketch, "E858", {"start": v(14.72, 0.47) * mm, "end": v(14.66, 0.57) * mm});
            skLineSegment(sketch, "E859", {"start": v(14.66, 0.57) * mm, "end": v(14.6, 0.66) * mm});
            skLineSegment(sketch, "E860", {"start": v(14.6, 0.66) * mm, "end": v(14.53, 0.75) * mm});
            skLineSegment(sketch, "E861", {"start": v(14.53, 0.75) * mm, "end": v(14.46, 0.84) * mm});
            skLineSegment(sketch, "E862", {"start": v(14.46, 0.84) * mm, "end": v(14.38, 0.92) * mm});
            skLineSegment(sketch, "E863", {"start": v(14.38, 0.92) * mm, "end": v(14.3, 1) * mm});
            skLineSegment(sketch, "E864", {"start": v(14.3, 1) * mm, "end": v(14.22, 1.08) * mm});
            skLineSegment(sketch, "E865", {"start": v(14.22, 1.08) * mm, "end": v(14.13, 1.15) * mm});
            skLineSegment(sketch, "E866", {"start": v(14.13, 1.15) * mm, "end": v(14.04, 1.22) * mm});
            skLineSegment(sketch, "E867", {"start": v(14.04, 1.22) * mm, "end": v(13.94, 1.28) * mm});
            skLineSegment(sketch, "E868", {"start": v(13.94, 1.28) * mm, "end": v(13.84, 1.34) * mm});
            skLineSegment(sketch, "E869", {"start": v(13.84, 1.34) * mm, "end": v(13.73, 1.4) * mm});
            skLineSegment(sketch, "E870", {"start": v(13.73, 1.4) * mm, "end": v(13.63, 1.45) * mm});
            skLineSegment(sketch, "E871", {"start": v(13.63, 1.45) * mm, "end": v(13.52, 1.5) * mm});
            skLineSegment(sketch, "E872", {"start": v(13.52, 1.5) * mm, "end": v(13.28, 1.57) * mm});
            skLineSegment(sketch, "E873", {"start": v(13.28, 1.57) * mm, "end": v(13.04, 1.63) * mm});
            skLineSegment(sketch, "E874", {"start": v(13.04, 1.63) * mm, "end": v(12.79, 1.66) * mm});
            skLineSegment(sketch, "E875", {"start": v(12.79, 1.66) * mm, "end": v(12.53, 1.67) * mm});
            skLineSegment(sketch, "E876", {"start": v(12.53, 1.67) * mm, "end": v(12.27, 1.66) * mm});
            skLineSegment(sketch, "E877", {"start": v(12.27, 1.66) * mm, "end": v(12.02, 1.63) * mm});
            skLineSegment(sketch, "E878", {"start": v(12.02, 1.63) * mm, "end": v(11.77, 1.57) * mm});
            skLineSegment(sketch, "E879", {"start": v(11.77, 1.57) * mm, "end": v(11.54, 1.49) * mm});
            skLineSegment(sketch, "E880", {"start": v(11.54, 1.49) * mm, "end": v(11.43, 1.44) * mm});
            skLineSegment(sketch, "E881", {"start": v(11.43, 1.44) * mm, "end": v(11.32, 1.39) * mm});
            skLineSegment(sketch, "E882", {"start": v(11.32, 1.39) * mm, "end": v(11.22, 1.33) * mm});
            skLineSegment(sketch, "E883", {"start": v(11.22, 1.33) * mm, "end": v(11.12, 1.27) * mm});
            skLineSegment(sketch, "E884", {"start": v(11.12, 1.27) * mm, "end": v(11.02, 1.2) * mm});
            skLineSegment(sketch, "E885", {"start": v(11.02, 1.2) * mm, "end": v(10.93, 1.14) * mm});
            skLineSegment(sketch, "E886", {"start": v(10.93, 1.14) * mm, "end": v(10.84, 1.07) * mm});
            skLineSegment(sketch, "E887", {"start": v(10.84, 1.07) * mm, "end": v(10.76, 1) * mm});
            skLineSegment(sketch, "E888", {"start": v(10.76, 1) * mm, "end": v(10.68, 0.91) * mm});
            skLineSegment(sketch, "E889", {"start": v(10.68, 0.91) * mm, "end": v(10.6, 0.83) * mm});
            skLineSegment(sketch, "E890", {"start": v(10.6, 0.83) * mm, "end": v(10.53, 0.74) * mm});
            skLineSegment(sketch, "E891", {"start": v(10.53, 0.74) * mm, "end": v(10.46, 0.65) * mm});
            skLineSegment(sketch, "E892", {"start": v(10.46, 0.65) * mm, "end": v(10.4, 0.56) * mm});
            skLineSegment(sketch, "E893", {"start": v(10.4, 0.56) * mm, "end": v(10.34, 0.47) * mm});
            skLineSegment(sketch, "E894", {"start": v(10.34, 0.47) * mm, "end": v(10.29, 0.37) * mm});
            skLineSegment(sketch, "E895", {"start": v(10.29, 0.37) * mm, "end": v(10.24, 0.26) * mm});
            skLineSegment(sketch, "E896", {"start": v(10.24, 0.26) * mm, "end": v(10.2, 0.16) * mm});
            skLineSegment(sketch, "E897", {"start": v(10.2, 0.16) * mm, "end": v(10.16, 0.05) * mm});
            skLineSegment(sketch, "E898", {"start": v(10.16, 0.05) * mm, "end": v(10.12, -0.06) * mm});
            skLineSegment(sketch, "E899", {"start": v(10.12, -0.06) * mm, "end": v(10.1, -0.17) * mm});
            skLineSegment(sketch, "E900", {"start": v(10.1, -0.17) * mm, "end": v(10.07, -0.29) * mm});
            skLineSegment(sketch, "E901", {"start": v(10.07, -0.29) * mm, "end": v(10.06, -0.4) * mm});
            skLineSegment(sketch, "E902", {"start": v(10.06, -0.4) * mm, "end": v(10.05, -0.52) * mm});
            skLineSegment(sketch, "E903", {"start": v(10.05, -0.52) * mm, "end": v(10.05, -0.65) * mm});
            skLineSegment(sketch, "E904", {"start": v(10.05, -0.65) * mm, "end": v(10.05, -0.76) * mm});
            skLineSegment(sketch, "E905", {"start": v(10.05, -0.76) * mm, "end": v(10.06, -0.88) * mm});
            skLineSegment(sketch, "E906", {"start": v(10.06, -0.88) * mm, "end": v(10.07, -0.99) * mm});
            skLineSegment(sketch, "E907", {"start": v(10.07, -0.99) * mm, "end": v(10.1, -1.1) * mm});
            skLineSegment(sketch, "E908", {"start": v(10.1, -1.1) * mm, "end": v(10.12, -1.2) * mm});
            skLineSegment(sketch, "E909", {"start": v(10.12, -1.2) * mm, "end": v(10.15, -1.32) * mm});
            skLineSegment(sketch, "E910", {"start": v(10.15, -1.32) * mm, "end": v(10.19, -1.42) * mm});
            skLineSegment(sketch, "E911", {"start": v(10.19, -1.42) * mm, "end": v(10.23, -1.53) * mm});
            skLineSegment(sketch, "E912", {"start": v(10.23, -1.53) * mm, "end": v(10.28, -1.63) * mm});
            skLineSegment(sketch, "E913", {"start": v(10.28, -1.63) * mm, "end": v(10.34, -1.73) * mm});
            skLineSegment(sketch, "E914", {"start": v(10.34, -1.73) * mm, "end": v(10.4, -1.83) * mm});
            skLineSegment(sketch, "E915", {"start": v(10.4, -1.83) * mm, "end": v(10.46, -1.92) * mm});
            skLineSegment(sketch, "E916", {"start": v(10.46, -1.92) * mm, "end": v(10.52, -2) * mm});
            skLineSegment(sketch, "E917", {"start": v(10.52, -2) * mm, "end": v(10.6, -2.1) * mm});
            skLineSegment(sketch, "E918", {"start": v(10.6, -2.1) * mm, "end": v(10.67, -2.18) * mm});
            skLineSegment(sketch, "E919", {"start": v(10.67, -2.18) * mm, "end": v(10.75, -2.26) * mm});
            skLineSegment(sketch, "E920", {"start": v(10.75, -2.26) * mm, "end": v(10.84, -2.33) * mm});
            skLineSegment(sketch, "E921", {"start": v(10.84, -2.33) * mm, "end": v(10.92, -2.4) * mm});
            skLineSegment(sketch, "E922", {"start": v(10.92, -2.4) * mm, "end": v(11.02, -2.47) * mm});
            skLineSegment(sketch, "E923", {"start": v(11.02, -2.47) * mm, "end": v(11.11, -2.53) * mm});
            skLineSegment(sketch, "E924", {"start": v(11.11, -2.53) * mm, "end": v(11.21, -2.6) * mm});
            skLineSegment(sketch, "E925", {"start": v(11.21, -2.6) * mm, "end": v(11.31, -2.65) * mm});
            skLineSegment(sketch, "E926", {"start": v(11.31, -2.65) * mm, "end": v(11.42, -2.7) * mm});
            skLineSegment(sketch, "E927", {"start": v(11.42, -2.7) * mm, "end": v(11.53, -2.75) * mm});
            skLineSegment(sketch, "E928", {"start": v(11.53, -2.75) * mm, "end": v(11.65, -2.79) * mm});
            skLineSegment(sketch, "E929", {"start": v(11.65, -2.79) * mm, "end": v(11.76, -2.82) * mm});
            skLineSegment(sketch, "E930", {"start": v(11.76, -2.82) * mm, "end": v(11.88, -2.85) * mm});
            skLineSegment(sketch, "E931", {"start": v(11.88, -2.85) * mm, "end": v(12, -2.88) * mm});
            skLineSegment(sketch, "E932", {"start": v(12, -2.88) * mm, "end": v(12.13, -2.9) * mm});
            skLineSegment(sketch, "E933", {"start": v(12.13, -2.9) * mm, "end": v(12.26, -2.91) * mm});
            skLineSegment(sketch, "E934", {"start": v(12.26, -2.91) * mm, "end": v(12.38, -2.92) * mm});
            skLineSegment(sketch, "E935", {"start": v(12.38, -2.92) * mm, "end": v(12.51, -2.92) * mm});
            skLineSegment(sketch, "E936", {"start": v(12.51, -2.92) * mm, "end": v(12.65, -2.92) * mm});
            skLineSegment(sketch, "E937", {"start": v(12.65, -2.92) * mm, "end": v(12.77, -2.91) * mm});
            skLineSegment(sketch, "E938", {"start": v(12.77, -2.91) * mm, "end": v(12.9, -2.9) * mm});
            skLineSegment(sketch, "E939", {"start": v(12.9, -2.9) * mm, "end": v(13.03, -2.88) * mm});
            skLineSegment(sketch, "E940", {"start": v(13.03, -2.88) * mm, "end": v(13.15, -2.85) * mm});
            skLineSegment(sketch, "E941", {"start": v(13.15, -2.85) * mm, "end": v(13.27, -2.82) * mm});
            skLineSegment(sketch, "E942", {"start": v(13.27, -2.82) * mm, "end": v(13.39, -2.78) * mm});
            skLineSegment(sketch, "E943", {"start": v(13.39, -2.78) * mm, "end": v(13.5, -2.74) * mm});
            skLineSegment(sketch, "E944", {"start": v(13.5, -2.74) * mm, "end": v(13.62, -2.7) * mm});
            skLineSegment(sketch, "E945", {"start": v(13.62, -2.7) * mm, "end": v(13.72, -2.64) * mm});
            skLineSegment(sketch, "E946", {"start": v(13.72, -2.64) * mm, "end": v(13.83, -2.58) * mm});
            skLineSegment(sketch, "E947", {"start": v(13.83, -2.58) * mm, "end": v(13.93, -2.52) * mm});
            skLineSegment(sketch, "E948", {"start": v(13.93, -2.52) * mm, "end": v(14.03, -2.46) * mm});
            skLineSegment(sketch, "E949", {"start": v(14.03, -2.46) * mm, "end": v(14.12, -2.4) * mm});
            skLineSegment(sketch, "E950", {"start": v(14.12, -2.4) * mm, "end": v(14.2, -2.32) * mm});
            skLineSegment(sketch, "E951", {"start": v(14.2, -2.32) * mm, "end": v(14.3, -2.24) * mm});
            skLineSegment(sketch, "E952", {"start": v(14.3, -2.24) * mm, "end": v(14.37, -2.16) * mm});
            skLineSegment(sketch, "E953", {"start": v(14.37, -2.16) * mm, "end": v(14.45, -2.08) * mm});
            skLineSegment(sketch, "E954", {"start": v(14.45, -2.08) * mm, "end": v(14.52, -2) * mm});
            skLineSegment(sketch, "E955", {"start": v(14.52, -2) * mm, "end": v(14.59, -1.9) * mm});
            skLineSegment(sketch, "E956", {"start": v(14.59, -1.9) * mm, "end": v(14.65, -1.81) * mm});
            skLineSegment(sketch, "E957", {"start": v(14.65, -1.81) * mm, "end": v(14.7, -1.72) * mm});
            skLineSegment(sketch, "E958", {"start": v(14.7, -1.72) * mm, "end": v(14.76, -1.62) * mm});
            skLineSegment(sketch, "E959", {"start": v(14.76, -1.62) * mm, "end": v(14.81, -1.52) * mm});
            skLineSegment(sketch, "E960", {"start": v(14.81, -1.52) * mm, "end": v(14.86, -1.41) * mm});
            skLineSegment(sketch, "E961", {"start": v(14.86, -1.41) * mm, "end": v(14.9, -1.3) * mm});
            skLineSegment(sketch, "E962", {"start": v(14.9, -1.3) * mm, "end": v(14.93, -1.2) * mm});
            skLineSegment(sketch, "E963", {"start": v(14.93, -1.2) * mm, "end": v(14.95, -1.08) * mm});
            skLineSegment(sketch, "E964", {"start": v(14.95, -1.08) * mm, "end": v(14.97, -0.97) * mm});
            skLineSegment(sketch, "E965", {"start": v(14.97, -0.97) * mm, "end": v(14.99, -0.85) * mm});
            skLineSegment(sketch, "E966", {"start": v(14.99, -0.85) * mm, "end": v(15, -0.73) * mm});
            skLineSegment(sketch, "E967", {"start": v(15, -0.73) * mm, "end": v(15, -0.61) * mm});
            skLineSegment(sketch, "E968", {"start": v(15, -0.61) * mm, "end": v(15, -0.5) * mm});
            skLineSegment(sketch, "E969", {"start": v(15, -0.5) * mm, "end": v(14.99, -0.38) * mm});
            skLineSegment(sketch, "E970", {"start": v(14.99, -0.38) * mm, "end": v(14.97, -0.27) * mm});
            skLineSegment(sketch, "E971", {"start": v(14.97, -0.27) * mm, "end": v(14.95, -0.15) * mm});
            skLineSegment(sketch, "E972", {"start": v(14.95, -0.15) * mm, "end": v(14.93, -0.04) * mm});
            skLineSegment(sketch, "E973", {"start": v(14.93, -0.04) * mm, "end": v(14.9, 0.06) * mm});
            skLineSegment(sketch, "E974", {"start": v(14.9, 0.06) * mm, "end": v(14.86, 0.17) * mm});
            skLineSegment(sketch, "E975", {"start": v(14.86, 0.17) * mm, "end": v(14.82, 0.28) * mm});
            skLineSegment(sketch, "E976", {"start": v(15.57, -3.5) * mm, "end": v(11.67, -3.5) * mm});
            skLineSegment(sketch, "E977", {"start": v(11.67, -3.5) * mm, "end": v(7.78, -3.5) * mm});
            skLineSegment(sketch, "E978", {"start": v(7.78, -3.5) * mm, "end": v(3.9, -3.5) * mm});
            skLineSegment(sketch, "E979", {"start": v(3.9, -3.5) * mm, "end": v(0, -3.5) * mm});
            skLineSegment(sketch, "E980", {"start": v(0, -3.5) * mm, "end": v(-3.9, -3.5) * mm});
            skLineSegment(sketch, "E981", {"start": v(-3.9, -3.5) * mm, "end": v(-7.78, -3.5) * mm});
            skLineSegment(sketch, "E982", {"start": v(-7.78, -3.5) * mm, "end": v(-11.67, -3.5) * mm});
            skLineSegment(sketch, "E983", {"start": v(-11.67, -3.5) * mm, "end": v(-15.57, -3.5) * mm});
            skLineSegment(sketch, "E984", {"start": v(-15.57, -3.5) * mm, "end": v(-15.57, -2.63) * mm});
            skLineSegment(sketch, "E985", {"start": v(-15.57, -2.63) * mm, "end": v(-15.57, -1.75) * mm});
            skLineSegment(sketch, "E986", {"start": v(-15.57, -1.75) * mm, "end": v(-15.57, -0.88) * mm});
            skLineSegment(sketch, "E987", {"start": v(-15.57, -0.88) * mm, "end": v(-15.57, 0) * mm});
            skLineSegment(sketch, "E988", {"start": v(-15.57, 0) * mm, "end": v(-15.57, 0.88) * mm});
            skLineSegment(sketch, "E989", {"start": v(-15.57, 0.88) * mm, "end": v(-15.57, 1.75) * mm});
            skLineSegment(sketch, "E990", {"start": v(-15.57, 1.75) * mm, "end": v(-15.57, 2.63) * mm});
            skLineSegment(sketch, "E991", {"start": v(-15.57, 2.63) * mm, "end": v(-15.57, 3.5) * mm});
            skLineSegment(sketch, "E992", {"start": v(-15.57, 3.5) * mm, "end": v(-11.67, 3.5) * mm});
            skLineSegment(sketch, "E993", {"start": v(-11.67, 3.5) * mm, "end": v(-7.78, 3.5) * mm});
            skLineSegment(sketch, "E994", {"start": v(-7.78, 3.5) * mm, "end": v(-3.9, 3.5) * mm});
            skLineSegment(sketch, "E995", {"start": v(-3.9, 3.5) * mm, "end": v(0, 3.5) * mm});
            skLineSegment(sketch, "E996", {"start": v(0, 3.5) * mm, "end": v(3.9, 3.5) * mm});
            skLineSegment(sketch, "E997", {"start": v(3.9, 3.5) * mm, "end": v(7.78, 3.5) * mm});
            skLineSegment(sketch, "E998", {"start": v(7.78, 3.5) * mm, "end": v(11.67, 3.5) * mm});
            skLineSegment(sketch, "E999", {"start": v(11.67, 3.5) * mm, "end": v(15.57, 3.5) * mm});
            skLineSegment(sketch, "E1000", {"start": v(15.57, 3.5) * mm, "end": v(15.57, 2.63) * mm});
            skLineSegment(sketch, "E1001", {"start": v(15.57, 2.63) * mm, "end": v(15.57, 1.75) * mm});
            skLineSegment(sketch, "E1002", {"start": v(15.57, 1.75) * mm, "end": v(15.57, 0.88) * mm});
            skLineSegment(sketch, "E1003", {"start": v(15.57, 0.88) * mm, "end": v(15.57, 0) * mm});
            skLineSegment(sketch, "E1004", {"start": v(15.57, 0) * mm, "end": v(15.57, -0.88) * mm});
            skLineSegment(sketch, "E1005", {"start": v(15.57, -0.88) * mm, "end": v(15.57, -1.75) * mm});
            skLineSegment(sketch, "E1006", {"start": v(15.57, -1.75) * mm, "end": v(15.57, -2.63) * mm});
            skLineSegment(sketch, "E1007", {"start": v(15.57, -2.63) * mm, "end": v(15.57, -3.5) * mm});
            skSolve(sketch);
        }
        {
            var Q0;
            Q0=makeQuery(id+"F0.imprint","IMPRINT",FACE,{"disambiguationData":[TD([[makeQuery(id+"F0.imprint","IMPRINT",EDGE,{"derivedFrom":sQuery(id+"F0.wireOp",EDGE,"E0")}),1.0]])]});
            var Q1;
            Q1=makeQuery(id+"F0.imprint","IMPRINT",FACE,{"disambiguationData":[TD([[makeQuery(id+"F0.imprint","IMPRINT",EDGE,{"derivedFrom":sQuery(id+"F0.wireOp",EDGE,"E48")}),1.0]])]});
            var Q2;
            Q2=makeQuery(id+"F0.imprint","IMPRINT",FACE,{"disambiguationData":[TD([[makeQuery(id+"F0.imprint","IMPRINT",EDGE,{"derivedFrom":sQuery(id+"F0.wireOp",EDGE,"E304")}),1.0]])]});
            var Q3;
            Q3=makeQuery(id+"F0.imprint","IMPRINT",FACE,{"disambiguationData":[TD([[makeQuery(id+"F0.imprint","IMPRINT",EDGE,{"derivedFrom":sQuery(id+"F0.wireOp",EDGE,"E440")}),1.0]])]});
            var Q4;
            Q4=makeQuery(id+"F0.imprint","IMPRINT",FACE,{"disambiguationData":[TD([[makeQuery(id+"F0.imprint","IMPRINT",EDGE,{"derivedFrom":sQuery(id+"F0.wireOp",EDGE,"E680")}),1.0]])]});
            var Q5;
            Q5=makeQuery(id+"F0.imprint","IMPRINT",FACE,{"disambiguationData":[TD([[makeQuery(id+"F0.imprint","IMPRINT",EDGE,{"derivedFrom":sQuery(id+"F0.wireOp",EDGE,"E736")}),1.0]])]});
            extrude(context, id + "F1", {"entities" : qUnion([Q0, Q1, Q2, Q3, Q4, Q5]), "depth" : 2 * mm, "offsetDistance" : 25 * mm});
        }
        {
            var Q0;
            Q0=makeQuery(id+"F0.imprint","IMPRINT",FACE,{"disambiguationData":[TD([[makeQuery(id+"F0.imprint","IMPRINT",EDGE,{"derivedFrom":sQuery(id+"F0.wireOp",EDGE,"E0")}),-1.0]])]});
            var Q1;
            Q1=makeQuery(id+"F0.imprint","IMPRINT",FACE,{"disambiguationData":[TD([[makeQuery(id+"F0.imprint","IMPRINT",EDGE,{"derivedFrom":sQuery(id+"F0.wireOp",EDGE,"E48")}),1.0]])]});
            var Q2;
            Q2=makeQuery(id+"F0.imprint","IMPRINT",FACE,{"disambiguationData":[TD([[makeQuery(id+"F0.imprint","IMPRINT",EDGE,{"derivedFrom":sQuery(id+"F0.wireOp",EDGE,"E0")}),1.0]])]});
            var Q3;
            Q3=makeQuery(id+"F0.imprint","IMPRINT",FACE,{"disambiguationData":[TD([[makeQuery(id+"F0.imprint","IMPRINT",EDGE,{"derivedFrom":sQuery(id+"F0.wireOp",EDGE,"E48")}),-1.0]])]});
            var Q4;
            Q4=makeQuery(id+"F0.imprint","IMPRINT",FACE,{"disambiguationData":[TD([[makeQuery(id+"F0.imprint","IMPRINT",EDGE,{"derivedFrom":sQuery(id+"F0.wireOp",EDGE,"E304")}),1.0]])]});
            var Q5;
            Q5=makeQuery(id+"F0.imprint","IMPRINT",FACE,{"disambiguationData":[TD([[makeQuery(id+"F0.imprint","IMPRINT",EDGE,{"derivedFrom":sQuery(id+"F0.wireOp",EDGE,"E440")}),1.0]])]});
            var Q6;
            Q6=makeQuery(id+"F0.imprint","IMPRINT",FACE,{"disambiguationData":[TD([[makeQuery(id+"F0.imprint","IMPRINT",EDGE,{"derivedFrom":sQuery(id+"F0.wireOp",EDGE,"E440")}),-1.0]])]});
            var Q7;
            Q7=makeQuery(id+"F0.imprint","IMPRINT",FACE,{"disambiguationData":[TD([[makeQuery(id+"F0.imprint","IMPRINT",EDGE,{"derivedFrom":sQuery(id+"F0.wireOp",EDGE,"E680")}),1.0]])]});
            var Q8;
            Q8=makeQuery(id+"F0.imprint","IMPRINT",FACE,{"disambiguationData":[TD([[makeQuery(id+"F0.imprint","IMPRINT",EDGE,{"derivedFrom":sQuery(id+"F0.wireOp",EDGE,"E736")}),1.0]])]});
            var Q9;
            Q9=makeQuery(id+"F0.imprint","IMPRINT",FACE,{"disambiguationData":[TD([[makeQuery(id+"F0.imprint","IMPRINT",EDGE,{"derivedFrom":sQuery(id+"F0.wireOp",EDGE,"E736")}),-1.0]])]});
            extrude(context, id + "F2", {"entities" : qUnion([Q0, Q1, Q2, Q3, Q4, Q5, Q6, Q7, Q8, Q9]), "operationType" : NewBodyOperationType.ADD, "oppositeDirection" : true, "depth" : 0.5 * mm, "offsetDistance" : 25 * mm});
        }
    });
